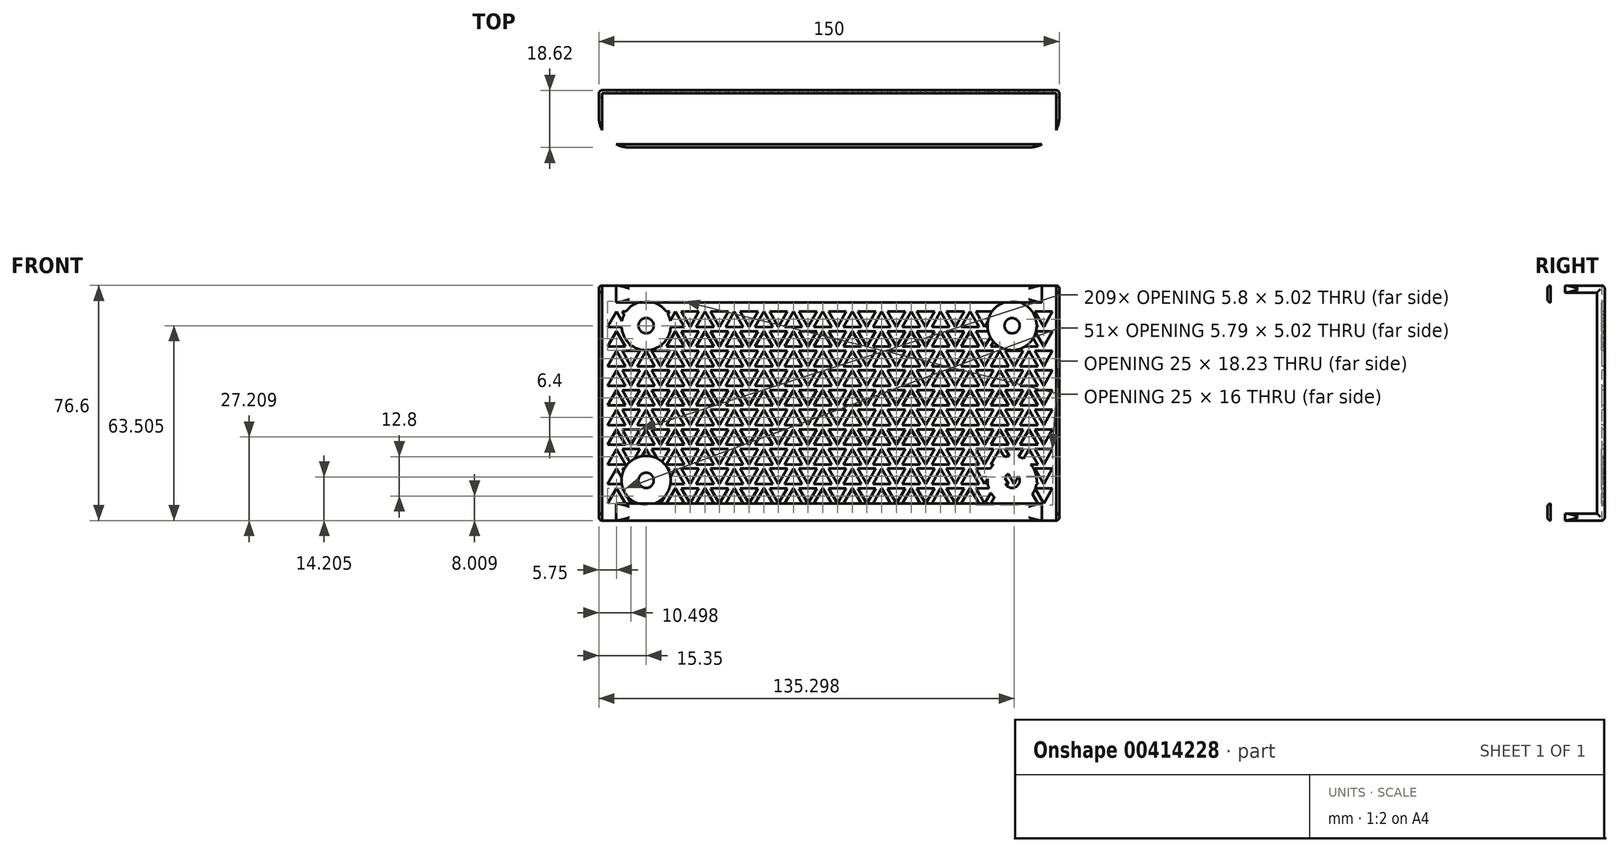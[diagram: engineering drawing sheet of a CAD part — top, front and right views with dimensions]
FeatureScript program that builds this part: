
annotation { "Feature Type Name" : "Feature", "Feature Type Description" : "" }
export const myFeature = defineFeature(function(context is Context, id is Id, definition is map)
    precondition{}
    {
        {
            var Q0;
            Q0=qCreatedBy(makeId("Right.planeOp"),FACE);
            var sketch = newSketch(context, id + "F0", { "sketchPlane" : qUnion([Q0])});
            skLineSegment(sketch, "E0", {"start": v(-14.28, -3.2) * mm, "end": v(-0.28, -3.2) * mm});
            skLineSegment(sketch, "E1", {"start": v(-0.28, -3.2) * mm, "end": v(-0.28, 68.8) * mm});
            skLineSegment(sketch, "E2", {"start": v(-14.28, -3.2) * mm, "end": v(-14.28, 0) * mm});
            skLineSegment(sketch, "E3", {"start": v(-0.28, 68.8) * mm, "end": v(2.22, 68.8) * mm});
            skLineSegment(sketch, "E4", {"start": v(2.22, 68.8) * mm, "end": v(2.22, -3.2) * mm});
            skLineSegment(sketch, "E5", {"start": v(2.22, -5.5) * mm, "end": v(-16.4, -5.5) * mm});
            skLineSegment(sketch, "E6", {"start": v(-16.4, -5.5) * mm, "end": v(-16.4, 0) * mm});
            skLineSegment(sketch, "E7", {"start": v(-16.4, 0) * mm, "end": v(-14.28, 0) * mm});
            skLineSegment(sketch, "E8", {"start": v(-0.28, -3.2) * mm, "end": v(2.22, -3.2) * mm});
            skLineSegment(sketch, "E9", {"start": v(-0.28, 32.8) * mm, "end": v(-25.27, 32.8) * mm, "construction": true});
            skPoint(sketch, "E9.endSnap0", {"position": v(-0.28, 32.8) * mm});
            skLineSegment(sketch, "E10", {"start": v(2.22, -3.2) * mm, "end": v(2.22, -5.5) * mm});
            skLineSegment(sketch, "E11.MirrorCS", {"start": v(-16.4, 71.1) * mm, "end": v(-16.4, 65.6) * mm});
            skLineSegment(sketch, "E12.MirrorCS", {"start": v(-16.4, 65.6) * mm, "end": v(-14.28, 65.6) * mm});
            skLineSegment(sketch, "E13.MirrorCS", {"start": v(-14.28, 68.8) * mm, "end": v(-14.28, 65.6) * mm});
            skLineSegment(sketch, "E14.MirrorCS", {"start": v(-14.28, 68.8) * mm, "end": v(-0.28, 68.8) * mm});
            skLineSegment(sketch, "E15.MirrorCS", {"start": v(2.22, 68.8) * mm, "end": v(2.22, 71.1) * mm});
            skLineSegment(sketch, "E16.MirrorCS", {"start": v(2.22, 71.1) * mm, "end": v(-16.4, 71.1) * mm});
            skSolve(sketch);
        }
        {
            var Q0;
            Q0=makeQuery(id+"F0.imprint","IMPRINT",FACE,{"disambiguationData":[TD([[makeQuery(id+"F0.imprint","IMPRINT",EDGE,{"derivedFrom":sQuery(id+"F0.wireOp",EDGE,"E0")}),-1.0]])]});
            var Q1;
            Q1=makeQuery(id+"F0.imprint","IMPRINT",FACE,{"disambiguationData":[TD([[makeQuery(id+"F0.imprint","IMPRINT",EDGE,{"derivedFrom":sQuery(id+"F0.wireOp",EDGE,"E1")}),-1.0]])]});
            var Q2;
            Q2=makeQuery(id+"F0.imprint","IMPRINT",FACE,{"disambiguationData":[TD([[makeQuery(id+"F0.imprint","IMPRINT",EDGE,{"derivedFrom":sQuery(id+"F0.wireOp",EDGE,"E11.MirrorCS")}),1.0]])]});
            extrude(context, id + "F1", {"entities" : qUnion([Q0, Q1, Q2]), "depth" : 150 * mm});
        }
        {
            var Q0;
            Q0=makeQuery(id+"F1.opExtrude","SWEPT_FACE",FACE,{"disambiguationData":[OSD([sQuery(id+"F0.wireOp",EDGE,"E4")])]});
            var sketch = newSketch(context, id + "F2", { "sketchPlane" : qUnion([Q0])});
            skCircle(sketch, "E17.MirrorC", {"center": v(-134.6, 58) * mm, "radius": 2.48 * mm});
            skCircle(sketch, "E18.MirrorC", {"center": v(-134.6, 58) * mm, "radius": 8 * mm});
            skLineSegment(sketch, "E19", {"start": v(0, 32.8) * mm, "end": v(-150, 32.8) * mm, "construction": true});
            skCircle(sketch, "E20.MirrorC", {"center": v(-134.6, 7.6) * mm, "radius": 8 * mm});
            skCircle(sketch, "E21.MirrorC", {"center": v(-134.6, 7.6) * mm, "radius": 2.48 * mm});
            skLineSegment(sketch, "E22", {"start": v(-75, 32.8) * mm, "end": v(-75, -18.93) * mm, "construction": true});
            skCircle(sketch, "E23.MirrorC", {"center": v(-15.4, 58) * mm, "radius": 2.48 * mm});
            skCircle(sketch, "E24.MirrorC", {"center": v(-15.4, 58) * mm, "radius": 8 * mm});
            skCircle(sketch, "E25.MirrorC", {"center": v(-15.4, 7.6) * mm, "radius": 2.48 * mm});
            skCircle(sketch, "E26.MirrorC", {"center": v(-15.4, 7.6) * mm, "radius": 8 * mm});
            skSolve(sketch);
        }
        {
            var Q0;
            {var subQ0=sQuery(id+"F0.wireOp",EDGE,"E1");Q0=makeQuery(id+"FQkC6kYxM6FwjvR_1.boolean.opBoolean","MERGE",FACE,{"derivedFrom":[makeQuery(id+"F1.opExtrude","SWEPT_FACE",FACE,{"disambiguationData":[OSD([subQ0])]}),makeQuery(id+"FQkC6kYxM6FwjvR_1.opExtrude","CAP_FACE",FACE,{"disambiguationData":[OSD([subQ0]),ownerDisambiguation([makeQuery(id+"F2.imprint","IMPRINT",EDGE,{"derivedFrom":sQuery(id+"F2.wireOp",EDGE,"f48PPpMc-yMvx-ferq-ZrUK-wZFvooTv5NzE.bottom")})])],"isStart":false}),makeQuery(id+"FQkC6kYxM6FwjvR_1.opExtrude","CAP_FACE",FACE,{"disambiguationData":[OSD([subQ0]),ownerDisambiguation([makeQuery(id+"F2.imprint","IMPRINT",EDGE,{"derivedFrom":sQuery(id+"F2.wireOp",EDGE,"981fdd8d-e6c7-4c50-9df8-fd8ac8e3de200.MirrorCS")})])],"isStart":false})]});}
            var sketch = newSketch(context, id + "F3", { "sketchPlane" : qUnion([Q0])});
            skLineSegment(sketch, "E27", {"start": v(2.85, 0) * mm, "end": v(8.65, 0) * mm});
            skLineSegment(sketch, "E28", {"start": v(8.65, 0) * mm, "end": v(5.75, 5.02) * mm});
            skLineSegment(sketch, "E29", {"start": v(5.75, 5.02) * mm, "end": v(2.85, 0) * mm});
            skLineSegment(sketch, "E30", {"start": v(7.6, 5.02) * mm, "end": v(13.4, 5.02) * mm});
            skLineSegment(sketch, "E31", {"start": v(13.4, 5.02) * mm, "end": v(10.5, 0) * mm});
            skLineSegment(sketch, "E32", {"start": v(10.5, 0) * mm, "end": v(7.6, 5.02) * mm});
            skLineSegment(sketch, "E33.0.1.0", {"start": v(2.85, 6.4) * mm, "end": v(8.65, 6.4) * mm});
            skLineSegment(sketch, "E33.0.1.1", {"start": v(8.65, 6.4) * mm, "end": v(5.75, 11.42) * mm});
            skLineSegment(sketch, "E33.0.1.2", {"start": v(5.75, 11.42) * mm, "end": v(2.85, 6.4) * mm});
            skLineSegment(sketch, "E33.0.1.3", {"start": v(10.5, 6.4) * mm, "end": v(7.6, 11.42) * mm});
            skLineSegment(sketch, "E33.0.1.4", {"start": v(13.4, 11.42) * mm, "end": v(10.5, 6.4) * mm});
            skLineSegment(sketch, "E33.0.1.5", {"start": v(7.6, 11.42) * mm, "end": v(13.4, 11.42) * mm});
            skLineSegment(sketch, "E33.0.2.0", {"start": v(2.85, 12.8) * mm, "end": v(8.65, 12.8) * mm});
            skLineSegment(sketch, "E33.0.2.1", {"start": v(8.65, 12.8) * mm, "end": v(5.75, 17.82) * mm});
            skLineSegment(sketch, "E33.0.2.2", {"start": v(5.75, 17.82) * mm, "end": v(2.85, 12.8) * mm});
            skLineSegment(sketch, "E33.0.2.3", {"start": v(10.5, 12.8) * mm, "end": v(7.6, 17.82) * mm});
            skLineSegment(sketch, "E33.0.2.4", {"start": v(13.4, 17.82) * mm, "end": v(10.5, 12.8) * mm});
            skLineSegment(sketch, "E33.0.2.5", {"start": v(7.6, 17.82) * mm, "end": v(13.4, 17.82) * mm});
            skLineSegment(sketch, "E33.0.3.0", {"start": v(2.85, 19.2) * mm, "end": v(8.65, 19.2) * mm});
            skLineSegment(sketch, "E33.0.3.1", {"start": v(8.65, 19.2) * mm, "end": v(5.75, 24.22) * mm});
            skLineSegment(sketch, "E33.0.3.2", {"start": v(5.75, 24.22) * mm, "end": v(2.85, 19.2) * mm});
            skLineSegment(sketch, "E33.0.3.3", {"start": v(10.5, 19.2) * mm, "end": v(7.6, 24.22) * mm});
            skLineSegment(sketch, "E33.0.3.4", {"start": v(13.4, 24.22) * mm, "end": v(10.5, 19.2) * mm});
            skLineSegment(sketch, "E33.0.3.5", {"start": v(7.6, 24.22) * mm, "end": v(13.4, 24.22) * mm});
            skLineSegment(sketch, "E33.0.4.0", {"start": v(2.85, 25.6) * mm, "end": v(8.65, 25.6) * mm});
            skLineSegment(sketch, "E33.0.4.1", {"start": v(8.65, 25.6) * mm, "end": v(5.75, 30.62) * mm});
            skLineSegment(sketch, "E33.0.4.2", {"start": v(5.75, 30.62) * mm, "end": v(2.85, 25.6) * mm});
            skLineSegment(sketch, "E33.0.4.3", {"start": v(10.5, 25.6) * mm, "end": v(7.6, 30.62) * mm});
            skLineSegment(sketch, "E33.0.4.4", {"start": v(13.4, 30.62) * mm, "end": v(10.5, 25.6) * mm});
            skLineSegment(sketch, "E33.0.4.5", {"start": v(7.6, 30.62) * mm, "end": v(13.4, 30.62) * mm});
            skLineSegment(sketch, "E33.0.5.0", {"start": v(2.85, 32) * mm, "end": v(8.65, 32) * mm});
            skLineSegment(sketch, "E33.0.5.1", {"start": v(8.65, 32) * mm, "end": v(5.75, 37.02) * mm});
            skLineSegment(sketch, "E33.0.5.2", {"start": v(5.75, 37.02) * mm, "end": v(2.85, 32) * mm});
            skLineSegment(sketch, "E33.0.5.3", {"start": v(10.5, 32) * mm, "end": v(7.6, 37.02) * mm});
            skLineSegment(sketch, "E33.0.5.4", {"start": v(13.4, 37.02) * mm, "end": v(10.5, 32) * mm});
            skLineSegment(sketch, "E33.0.5.5", {"start": v(7.6, 37.02) * mm, "end": v(13.4, 37.02) * mm});
            skLineSegment(sketch, "E33.0.6.0", {"start": v(2.85, 38.4) * mm, "end": v(8.65, 38.4) * mm});
            skLineSegment(sketch, "E33.0.6.1", {"start": v(8.65, 38.4) * mm, "end": v(5.75, 43.42) * mm});
            skLineSegment(sketch, "E33.0.6.2", {"start": v(5.75, 43.42) * mm, "end": v(2.85, 38.4) * mm});
            skLineSegment(sketch, "E33.0.6.3", {"start": v(10.5, 38.4) * mm, "end": v(7.6, 43.42) * mm});
            skLineSegment(sketch, "E33.0.6.4", {"start": v(13.4, 43.42) * mm, "end": v(10.5, 38.4) * mm});
            skLineSegment(sketch, "E33.0.6.5", {"start": v(7.6, 43.42) * mm, "end": v(13.4, 43.42) * mm});
            skLineSegment(sketch, "E33.0.7.0", {"start": v(2.85, 44.8) * mm, "end": v(8.65, 44.8) * mm});
            skLineSegment(sketch, "E33.0.7.1", {"start": v(8.65, 44.8) * mm, "end": v(5.75, 49.82) * mm});
            skLineSegment(sketch, "E33.0.7.2", {"start": v(5.75, 49.82) * mm, "end": v(2.85, 44.8) * mm});
            skLineSegment(sketch, "E33.0.7.3", {"start": v(10.5, 44.8) * mm, "end": v(7.6, 49.82) * mm});
            skLineSegment(sketch, "E33.0.7.4", {"start": v(13.4, 49.82) * mm, "end": v(10.5, 44.8) * mm});
            skLineSegment(sketch, "E33.0.7.5", {"start": v(7.6, 49.82) * mm, "end": v(13.4, 49.82) * mm});
            skLineSegment(sketch, "E33.0.8.0", {"start": v(2.85, 51.2) * mm, "end": v(8.65, 51.2) * mm});
            skLineSegment(sketch, "E33.0.8.1", {"start": v(8.65, 51.2) * mm, "end": v(5.75, 56.22) * mm});
            skLineSegment(sketch, "E33.0.8.2", {"start": v(5.75, 56.22) * mm, "end": v(2.85, 51.2) * mm});
            skLineSegment(sketch, "E33.0.8.3", {"start": v(10.5, 51.2) * mm, "end": v(7.6, 56.22) * mm});
            skLineSegment(sketch, "E33.0.8.4", {"start": v(13.4, 56.22) * mm, "end": v(10.5, 51.2) * mm});
            skLineSegment(sketch, "E33.0.8.5", {"start": v(7.6, 56.22) * mm, "end": v(13.4, 56.22) * mm});
            skLineSegment(sketch, "E33.0.9.0", {"start": v(2.85, 57.6) * mm, "end": v(8.65, 57.6) * mm});
            skLineSegment(sketch, "E33.0.9.1", {"start": v(8.65, 57.6) * mm, "end": v(5.75, 62.62) * mm});
            skLineSegment(sketch, "E33.0.9.2", {"start": v(5.75, 62.62) * mm, "end": v(2.85, 57.6) * mm});
            skLineSegment(sketch, "E33.0.9.3", {"start": v(10.5, 57.6) * mm, "end": v(7.6, 62.62) * mm});
            skLineSegment(sketch, "E33.0.9.4", {"start": v(13.4, 62.62) * mm, "end": v(10.5, 57.6) * mm});
            skLineSegment(sketch, "E33.0.9.5", {"start": v(7.6, 62.62) * mm, "end": v(13.4, 62.62) * mm});
            skLineSegment(sketch, "E33.1.0.0", {"start": v(12.45, 0) * mm, "end": v(18.25, 0) * mm});
            skLineSegment(sketch, "E33.1.0.1", {"start": v(18.25, 0) * mm, "end": v(15.35, 5.02) * mm});
            skLineSegment(sketch, "E33.1.0.2", {"start": v(15.35, 5.02) * mm, "end": v(12.45, 0) * mm});
            skLineSegment(sketch, "E33.1.0.3", {"start": v(20.1, 0) * mm, "end": v(17.2, 5.02) * mm});
            skLineSegment(sketch, "E33.1.0.4", {"start": v(23, 5.02) * mm, "end": v(20.1, 0) * mm});
            skLineSegment(sketch, "E33.1.0.5", {"start": v(17.2, 5.02) * mm, "end": v(23, 5.02) * mm});
            skLineSegment(sketch, "E33.1.1.0", {"start": v(12.45, 6.4) * mm, "end": v(18.25, 6.4) * mm});
            skLineSegment(sketch, "E33.1.1.1", {"start": v(18.25, 6.4) * mm, "end": v(15.35, 11.42) * mm});
            skLineSegment(sketch, "E33.1.1.2", {"start": v(15.35, 11.42) * mm, "end": v(12.45, 6.4) * mm});
            skLineSegment(sketch, "E33.1.1.3", {"start": v(20.1, 6.4) * mm, "end": v(17.2, 11.42) * mm});
            skLineSegment(sketch, "E33.1.1.4", {"start": v(23, 11.42) * mm, "end": v(20.1, 6.4) * mm});
            skLineSegment(sketch, "E33.1.1.5", {"start": v(17.2, 11.42) * mm, "end": v(23, 11.42) * mm});
            skLineSegment(sketch, "E33.1.2.0", {"start": v(12.45, 12.8) * mm, "end": v(18.25, 12.8) * mm});
            skLineSegment(sketch, "E33.1.2.1", {"start": v(18.25, 12.8) * mm, "end": v(15.35, 17.82) * mm});
            skLineSegment(sketch, "E33.1.2.2", {"start": v(15.35, 17.82) * mm, "end": v(12.45, 12.8) * mm});
            skLineSegment(sketch, "E33.1.2.3", {"start": v(20.1, 12.8) * mm, "end": v(17.2, 17.82) * mm});
            skLineSegment(sketch, "E33.1.2.4", {"start": v(23, 17.82) * mm, "end": v(20.1, 12.8) * mm});
            skLineSegment(sketch, "E33.1.2.5", {"start": v(17.2, 17.82) * mm, "end": v(23, 17.82) * mm});
            skLineSegment(sketch, "E33.1.3.0", {"start": v(12.45, 19.2) * mm, "end": v(18.25, 19.2) * mm});
            skLineSegment(sketch, "E33.1.3.1", {"start": v(18.25, 19.2) * mm, "end": v(15.35, 24.22) * mm});
            skLineSegment(sketch, "E33.1.3.2", {"start": v(15.35, 24.22) * mm, "end": v(12.45, 19.2) * mm});
            skLineSegment(sketch, "E33.1.3.3", {"start": v(20.1, 19.2) * mm, "end": v(17.2, 24.22) * mm});
            skLineSegment(sketch, "E33.1.3.4", {"start": v(23, 24.22) * mm, "end": v(20.1, 19.2) * mm});
            skLineSegment(sketch, "E33.1.3.5", {"start": v(17.2, 24.22) * mm, "end": v(23, 24.22) * mm});
            skLineSegment(sketch, "E33.1.4.0", {"start": v(12.45, 25.6) * mm, "end": v(18.25, 25.6) * mm});
            skLineSegment(sketch, "E33.1.4.1", {"start": v(18.25, 25.6) * mm, "end": v(15.35, 30.62) * mm});
            skLineSegment(sketch, "E33.1.4.2", {"start": v(15.35, 30.62) * mm, "end": v(12.45, 25.6) * mm});
            skLineSegment(sketch, "E33.1.4.3", {"start": v(20.1, 25.6) * mm, "end": v(17.2, 30.62) * mm});
            skLineSegment(sketch, "E33.1.4.4", {"start": v(23, 30.62) * mm, "end": v(20.1, 25.6) * mm});
            skLineSegment(sketch, "E33.1.4.5", {"start": v(17.2, 30.62) * mm, "end": v(23, 30.62) * mm});
            skLineSegment(sketch, "E33.1.5.0", {"start": v(12.45, 32) * mm, "end": v(18.25, 32) * mm});
            skLineSegment(sketch, "E33.1.5.1", {"start": v(18.25, 32) * mm, "end": v(15.35, 37.02) * mm});
            skLineSegment(sketch, "E33.1.5.2", {"start": v(15.35, 37.02) * mm, "end": v(12.45, 32) * mm});
            skLineSegment(sketch, "E33.1.5.3", {"start": v(20.1, 32) * mm, "end": v(17.2, 37.02) * mm});
            skLineSegment(sketch, "E33.1.5.4", {"start": v(23, 37.02) * mm, "end": v(20.1, 32) * mm});
            skLineSegment(sketch, "E33.1.5.5", {"start": v(17.2, 37.02) * mm, "end": v(23, 37.02) * mm});
            skLineSegment(sketch, "E33.1.6.0", {"start": v(12.45, 38.4) * mm, "end": v(18.25, 38.4) * mm});
            skLineSegment(sketch, "E33.1.6.1", {"start": v(18.25, 38.4) * mm, "end": v(15.35, 43.42) * mm});
            skLineSegment(sketch, "E33.1.6.2", {"start": v(15.35, 43.42) * mm, "end": v(12.45, 38.4) * mm});
            skLineSegment(sketch, "E33.1.6.3", {"start": v(20.1, 38.4) * mm, "end": v(17.2, 43.42) * mm});
            skLineSegment(sketch, "E33.1.6.4", {"start": v(23, 43.42) * mm, "end": v(20.1, 38.4) * mm});
            skLineSegment(sketch, "E33.1.6.5", {"start": v(17.2, 43.42) * mm, "end": v(23, 43.42) * mm});
            skLineSegment(sketch, "E33.1.7.0", {"start": v(12.45, 44.8) * mm, "end": v(18.25, 44.8) * mm});
            skLineSegment(sketch, "E33.1.7.1", {"start": v(18.25, 44.8) * mm, "end": v(15.35, 49.82) * mm});
            skLineSegment(sketch, "E33.1.7.2", {"start": v(15.35, 49.82) * mm, "end": v(12.45, 44.8) * mm});
            skLineSegment(sketch, "E33.1.7.3", {"start": v(20.1, 44.8) * mm, "end": v(17.2, 49.82) * mm});
            skLineSegment(sketch, "E33.1.7.4", {"start": v(23, 49.82) * mm, "end": v(20.1, 44.8) * mm});
            skLineSegment(sketch, "E33.1.7.5", {"start": v(17.2, 49.82) * mm, "end": v(23, 49.82) * mm});
            skLineSegment(sketch, "E33.1.8.0", {"start": v(12.45, 51.2) * mm, "end": v(18.25, 51.2) * mm});
            skLineSegment(sketch, "E33.1.8.1", {"start": v(18.25, 51.2) * mm, "end": v(15.35, 56.22) * mm});
            skLineSegment(sketch, "E33.1.8.2", {"start": v(15.35, 56.22) * mm, "end": v(12.45, 51.2) * mm});
            skLineSegment(sketch, "E33.1.8.3", {"start": v(20.1, 51.2) * mm, "end": v(17.2, 56.22) * mm});
            skLineSegment(sketch, "E33.1.8.4", {"start": v(23, 56.22) * mm, "end": v(20.1, 51.2) * mm});
            skLineSegment(sketch, "E33.1.8.5", {"start": v(17.2, 56.22) * mm, "end": v(23, 56.22) * mm});
            skLineSegment(sketch, "E33.1.9.0", {"start": v(12.45, 57.6) * mm, "end": v(18.25, 57.6) * mm});
            skLineSegment(sketch, "E33.1.9.1", {"start": v(18.25, 57.6) * mm, "end": v(15.35, 62.62) * mm});
            skLineSegment(sketch, "E33.1.9.2", {"start": v(15.35, 62.62) * mm, "end": v(12.45, 57.6) * mm});
            skLineSegment(sketch, "E33.1.9.3", {"start": v(20.1, 57.6) * mm, "end": v(17.2, 62.62) * mm});
            skLineSegment(sketch, "E33.1.9.4", {"start": v(23, 62.62) * mm, "end": v(20.1, 57.6) * mm});
            skLineSegment(sketch, "E33.1.9.5", {"start": v(17.2, 62.62) * mm, "end": v(23, 62.62) * mm});
            skLineSegment(sketch, "E33.2.0.0", {"start": v(22.05, 0) * mm, "end": v(27.85, 0) * mm});
            skLineSegment(sketch, "E33.2.0.1", {"start": v(27.85, 0) * mm, "end": v(24.95, 5.02) * mm});
            skLineSegment(sketch, "E33.2.0.2", {"start": v(24.95, 5.02) * mm, "end": v(22.05, 0) * mm});
            skLineSegment(sketch, "E33.2.0.3", {"start": v(29.7, 0) * mm, "end": v(26.8, 5.02) * mm});
            skLineSegment(sketch, "E33.2.0.4", {"start": v(32.6, 5.02) * mm, "end": v(29.7, 0) * mm});
            skLineSegment(sketch, "E33.2.0.5", {"start": v(26.8, 5.02) * mm, "end": v(32.6, 5.02) * mm});
            skLineSegment(sketch, "E33.2.1.0", {"start": v(22.05, 6.4) * mm, "end": v(27.85, 6.4) * mm});
            skLineSegment(sketch, "E33.2.1.1", {"start": v(27.85, 6.4) * mm, "end": v(24.95, 11.42) * mm});
            skLineSegment(sketch, "E33.2.1.2", {"start": v(24.95, 11.42) * mm, "end": v(22.05, 6.4) * mm});
            skLineSegment(sketch, "E33.2.1.3", {"start": v(29.7, 6.4) * mm, "end": v(26.8, 11.42) * mm});
            skLineSegment(sketch, "E33.2.1.4", {"start": v(32.6, 11.42) * mm, "end": v(29.7, 6.4) * mm});
            skLineSegment(sketch, "E33.2.1.5", {"start": v(26.8, 11.42) * mm, "end": v(32.6, 11.42) * mm});
            skLineSegment(sketch, "E33.2.2.0", {"start": v(22.05, 12.8) * mm, "end": v(27.85, 12.8) * mm});
            skLineSegment(sketch, "E33.2.2.1", {"start": v(27.85, 12.8) * mm, "end": v(24.95, 17.82) * mm});
            skLineSegment(sketch, "E33.2.2.2", {"start": v(24.95, 17.82) * mm, "end": v(22.05, 12.8) * mm});
            skLineSegment(sketch, "E33.2.2.3", {"start": v(29.7, 12.8) * mm, "end": v(26.8, 17.82) * mm});
            skLineSegment(sketch, "E33.2.2.4", {"start": v(32.6, 17.82) * mm, "end": v(29.7, 12.8) * mm});
            skLineSegment(sketch, "E33.2.2.5", {"start": v(26.8, 17.82) * mm, "end": v(32.6, 17.82) * mm});
            skLineSegment(sketch, "E33.2.3.0", {"start": v(22.05, 19.2) * mm, "end": v(27.85, 19.2) * mm});
            skLineSegment(sketch, "E33.2.3.1", {"start": v(27.85, 19.2) * mm, "end": v(24.95, 24.22) * mm});
            skLineSegment(sketch, "E33.2.3.2", {"start": v(24.95, 24.22) * mm, "end": v(22.05, 19.2) * mm});
            skLineSegment(sketch, "E33.2.3.3", {"start": v(29.7, 19.2) * mm, "end": v(26.8, 24.22) * mm});
            skLineSegment(sketch, "E33.2.3.4", {"start": v(32.6, 24.22) * mm, "end": v(29.7, 19.2) * mm});
            skLineSegment(sketch, "E33.2.3.5", {"start": v(26.8, 24.22) * mm, "end": v(32.6, 24.22) * mm});
            skLineSegment(sketch, "E33.2.4.0", {"start": v(22.05, 25.6) * mm, "end": v(27.85, 25.6) * mm});
            skLineSegment(sketch, "E33.2.4.1", {"start": v(27.85, 25.6) * mm, "end": v(24.95, 30.62) * mm});
            skLineSegment(sketch, "E33.2.4.2", {"start": v(24.95, 30.62) * mm, "end": v(22.05, 25.6) * mm});
            skLineSegment(sketch, "E33.2.4.3", {"start": v(29.7, 25.6) * mm, "end": v(26.8, 30.62) * mm});
            skLineSegment(sketch, "E33.2.4.4", {"start": v(32.6, 30.62) * mm, "end": v(29.7, 25.6) * mm});
            skLineSegment(sketch, "E33.2.4.5", {"start": v(26.8, 30.62) * mm, "end": v(32.6, 30.62) * mm});
            skLineSegment(sketch, "E33.2.5.0", {"start": v(22.05, 32) * mm, "end": v(27.85, 32) * mm});
            skLineSegment(sketch, "E33.2.5.1", {"start": v(27.85, 32) * mm, "end": v(24.95, 37.02) * mm});
            skLineSegment(sketch, "E33.2.5.2", {"start": v(24.95, 37.02) * mm, "end": v(22.05, 32) * mm});
            skLineSegment(sketch, "E33.2.5.3", {"start": v(29.7, 32) * mm, "end": v(26.8, 37.02) * mm});
            skLineSegment(sketch, "E33.2.5.4", {"start": v(32.6, 37.02) * mm, "end": v(29.7, 32) * mm});
            skLineSegment(sketch, "E33.2.5.5", {"start": v(26.8, 37.02) * mm, "end": v(32.6, 37.02) * mm});
            skLineSegment(sketch, "E33.2.6.0", {"start": v(22.05, 38.4) * mm, "end": v(27.85, 38.4) * mm});
            skLineSegment(sketch, "E33.2.6.1", {"start": v(27.85, 38.4) * mm, "end": v(24.95, 43.42) * mm});
            skLineSegment(sketch, "E33.2.6.2", {"start": v(24.95, 43.42) * mm, "end": v(22.05, 38.4) * mm});
            skLineSegment(sketch, "E33.2.6.3", {"start": v(29.7, 38.4) * mm, "end": v(26.8, 43.42) * mm});
            skLineSegment(sketch, "E33.2.6.4", {"start": v(32.6, 43.42) * mm, "end": v(29.7, 38.4) * mm});
            skLineSegment(sketch, "E33.2.6.5", {"start": v(26.8, 43.42) * mm, "end": v(32.6, 43.42) * mm});
            skLineSegment(sketch, "E33.2.7.0", {"start": v(22.05, 44.8) * mm, "end": v(27.85, 44.8) * mm});
            skLineSegment(sketch, "E33.2.7.1", {"start": v(27.85, 44.8) * mm, "end": v(24.95, 49.82) * mm});
            skLineSegment(sketch, "E33.2.7.2", {"start": v(24.95, 49.82) * mm, "end": v(22.05, 44.8) * mm});
            skLineSegment(sketch, "E33.2.7.3", {"start": v(29.7, 44.8) * mm, "end": v(26.8, 49.82) * mm});
            skLineSegment(sketch, "E33.2.7.4", {"start": v(32.6, 49.82) * mm, "end": v(29.7, 44.8) * mm});
            skLineSegment(sketch, "E33.2.7.5", {"start": v(26.8, 49.82) * mm, "end": v(32.6, 49.82) * mm});
            skLineSegment(sketch, "E33.2.8.0", {"start": v(22.05, 51.2) * mm, "end": v(27.85, 51.2) * mm});
            skLineSegment(sketch, "E33.2.8.1", {"start": v(27.85, 51.2) * mm, "end": v(24.95, 56.22) * mm});
            skLineSegment(sketch, "E33.2.8.2", {"start": v(24.95, 56.22) * mm, "end": v(22.05, 51.2) * mm});
            skLineSegment(sketch, "E33.2.8.3", {"start": v(29.7, 51.2) * mm, "end": v(26.8, 56.22) * mm});
            skLineSegment(sketch, "E33.2.8.4", {"start": v(32.6, 56.22) * mm, "end": v(29.7, 51.2) * mm});
            skLineSegment(sketch, "E33.2.8.5", {"start": v(26.8, 56.22) * mm, "end": v(32.6, 56.22) * mm});
            skLineSegment(sketch, "E33.2.9.0", {"start": v(22.05, 57.6) * mm, "end": v(27.85, 57.6) * mm});
            skLineSegment(sketch, "E33.2.9.1", {"start": v(27.85, 57.6) * mm, "end": v(24.95, 62.62) * mm});
            skLineSegment(sketch, "E33.2.9.2", {"start": v(24.95, 62.62) * mm, "end": v(22.05, 57.6) * mm});
            skLineSegment(sketch, "E33.2.9.3", {"start": v(29.7, 57.6) * mm, "end": v(26.8, 62.62) * mm});
            skLineSegment(sketch, "E33.2.9.4", {"start": v(32.6, 62.62) * mm, "end": v(29.7, 57.6) * mm});
            skLineSegment(sketch, "E33.2.9.5", {"start": v(26.8, 62.62) * mm, "end": v(32.6, 62.62) * mm});
            skLineSegment(sketch, "E33.3.0.0", {"start": v(31.65, 0) * mm, "end": v(37.45, 0) * mm});
            skLineSegment(sketch, "E33.3.0.1", {"start": v(37.45, 0) * mm, "end": v(34.55, 5.02) * mm});
            skLineSegment(sketch, "E33.3.0.2", {"start": v(34.55, 5.02) * mm, "end": v(31.65, 0) * mm});
            skLineSegment(sketch, "E33.3.0.3", {"start": v(39.3, 0) * mm, "end": v(36.4, 5.02) * mm});
            skLineSegment(sketch, "E33.3.0.4", {"start": v(42.2, 5.02) * mm, "end": v(39.3, 0) * mm});
            skLineSegment(sketch, "E33.3.0.5", {"start": v(36.4, 5.02) * mm, "end": v(42.2, 5.02) * mm});
            skLineSegment(sketch, "E33.3.1.0", {"start": v(31.65, 6.4) * mm, "end": v(37.45, 6.4) * mm});
            skLineSegment(sketch, "E33.3.1.1", {"start": v(37.45, 6.4) * mm, "end": v(34.55, 11.42) * mm});
            skLineSegment(sketch, "E33.3.1.2", {"start": v(34.55, 11.42) * mm, "end": v(31.65, 6.4) * mm});
            skLineSegment(sketch, "E33.3.1.3", {"start": v(39.3, 6.4) * mm, "end": v(36.4, 11.42) * mm});
            skLineSegment(sketch, "E33.3.1.4", {"start": v(42.2, 11.42) * mm, "end": v(39.3, 6.4) * mm});
            skLineSegment(sketch, "E33.3.1.5", {"start": v(36.4, 11.42) * mm, "end": v(42.2, 11.42) * mm});
            skLineSegment(sketch, "E33.3.2.0", {"start": v(31.65, 12.8) * mm, "end": v(37.45, 12.8) * mm});
            skLineSegment(sketch, "E33.3.2.1", {"start": v(37.45, 12.8) * mm, "end": v(34.55, 17.82) * mm});
            skLineSegment(sketch, "E33.3.2.2", {"start": v(34.55, 17.82) * mm, "end": v(31.65, 12.8) * mm});
            skLineSegment(sketch, "E33.3.2.3", {"start": v(39.3, 12.8) * mm, "end": v(36.4, 17.82) * mm});
            skLineSegment(sketch, "E33.3.2.4", {"start": v(42.2, 17.82) * mm, "end": v(39.3, 12.8) * mm});
            skLineSegment(sketch, "E33.3.2.5", {"start": v(36.4, 17.82) * mm, "end": v(42.2, 17.82) * mm});
            skLineSegment(sketch, "E33.3.3.0", {"start": v(31.65, 19.2) * mm, "end": v(37.45, 19.2) * mm});
            skLineSegment(sketch, "E33.3.3.1", {"start": v(37.45, 19.2) * mm, "end": v(34.55, 24.22) * mm});
            skLineSegment(sketch, "E33.3.3.2", {"start": v(34.55, 24.22) * mm, "end": v(31.65, 19.2) * mm});
            skLineSegment(sketch, "E33.3.3.3", {"start": v(39.3, 19.2) * mm, "end": v(36.4, 24.22) * mm});
            skLineSegment(sketch, "E33.3.3.4", {"start": v(42.2, 24.22) * mm, "end": v(39.3, 19.2) * mm});
            skLineSegment(sketch, "E33.3.3.5", {"start": v(36.4, 24.22) * mm, "end": v(42.2, 24.22) * mm});
            skLineSegment(sketch, "E33.3.4.0", {"start": v(31.65, 25.6) * mm, "end": v(37.45, 25.6) * mm});
            skLineSegment(sketch, "E33.3.4.1", {"start": v(37.45, 25.6) * mm, "end": v(34.55, 30.62) * mm});
            skLineSegment(sketch, "E33.3.4.2", {"start": v(34.55, 30.62) * mm, "end": v(31.65, 25.6) * mm});
            skLineSegment(sketch, "E33.3.4.3", {"start": v(39.3, 25.6) * mm, "end": v(36.4, 30.62) * mm});
            skLineSegment(sketch, "E33.3.4.4", {"start": v(42.2, 30.62) * mm, "end": v(39.3, 25.6) * mm});
            skLineSegment(sketch, "E33.3.4.5", {"start": v(36.4, 30.62) * mm, "end": v(42.2, 30.62) * mm});
            skLineSegment(sketch, "E33.3.5.0", {"start": v(31.65, 32) * mm, "end": v(37.45, 32) * mm});
            skLineSegment(sketch, "E33.3.5.1", {"start": v(37.45, 32) * mm, "end": v(34.55, 37.02) * mm});
            skLineSegment(sketch, "E33.3.5.2", {"start": v(34.55, 37.02) * mm, "end": v(31.65, 32) * mm});
            skLineSegment(sketch, "E33.3.5.3", {"start": v(39.3, 32) * mm, "end": v(36.4, 37.02) * mm});
            skLineSegment(sketch, "E33.3.5.4", {"start": v(42.2, 37.02) * mm, "end": v(39.3, 32) * mm});
            skLineSegment(sketch, "E33.3.5.5", {"start": v(36.4, 37.02) * mm, "end": v(42.2, 37.02) * mm});
            skLineSegment(sketch, "E33.3.6.0", {"start": v(31.65, 38.4) * mm, "end": v(37.45, 38.4) * mm});
            skLineSegment(sketch, "E33.3.6.1", {"start": v(37.45, 38.4) * mm, "end": v(34.55, 43.42) * mm});
            skLineSegment(sketch, "E33.3.6.2", {"start": v(34.55, 43.42) * mm, "end": v(31.65, 38.4) * mm});
            skLineSegment(sketch, "E33.3.6.3", {"start": v(39.3, 38.4) * mm, "end": v(36.4, 43.42) * mm});
            skLineSegment(sketch, "E33.3.6.4", {"start": v(42.2, 43.42) * mm, "end": v(39.3, 38.4) * mm});
            skLineSegment(sketch, "E33.3.6.5", {"start": v(36.4, 43.42) * mm, "end": v(42.2, 43.42) * mm});
            skLineSegment(sketch, "E33.3.7.0", {"start": v(31.65, 44.8) * mm, "end": v(37.45, 44.8) * mm});
            skLineSegment(sketch, "E33.3.7.1", {"start": v(37.45, 44.8) * mm, "end": v(34.55, 49.82) * mm});
            skLineSegment(sketch, "E33.3.7.2", {"start": v(34.55, 49.82) * mm, "end": v(31.65, 44.8) * mm});
            skLineSegment(sketch, "E33.3.7.3", {"start": v(39.3, 44.8) * mm, "end": v(36.4, 49.82) * mm});
            skLineSegment(sketch, "E33.3.7.4", {"start": v(42.2, 49.82) * mm, "end": v(39.3, 44.8) * mm});
            skLineSegment(sketch, "E33.3.7.5", {"start": v(36.4, 49.82) * mm, "end": v(42.2, 49.82) * mm});
            skLineSegment(sketch, "E33.3.8.0", {"start": v(31.65, 51.2) * mm, "end": v(37.45, 51.2) * mm});
            skLineSegment(sketch, "E33.3.8.1", {"start": v(37.45, 51.2) * mm, "end": v(34.55, 56.22) * mm});
            skLineSegment(sketch, "E33.3.8.2", {"start": v(34.55, 56.22) * mm, "end": v(31.65, 51.2) * mm});
            skLineSegment(sketch, "E33.3.8.3", {"start": v(39.3, 51.2) * mm, "end": v(36.4, 56.22) * mm});
            skLineSegment(sketch, "E33.3.8.4", {"start": v(42.2, 56.22) * mm, "end": v(39.3, 51.2) * mm});
            skLineSegment(sketch, "E33.3.8.5", {"start": v(36.4, 56.22) * mm, "end": v(42.2, 56.22) * mm});
            skLineSegment(sketch, "E33.3.9.0", {"start": v(31.65, 57.6) * mm, "end": v(37.45, 57.6) * mm});
            skLineSegment(sketch, "E33.3.9.1", {"start": v(37.45, 57.6) * mm, "end": v(34.55, 62.62) * mm});
            skLineSegment(sketch, "E33.3.9.2", {"start": v(34.55, 62.62) * mm, "end": v(31.65, 57.6) * mm});
            skLineSegment(sketch, "E33.3.9.3", {"start": v(39.3, 57.6) * mm, "end": v(36.4, 62.62) * mm});
            skLineSegment(sketch, "E33.3.9.4", {"start": v(42.2, 62.62) * mm, "end": v(39.3, 57.6) * mm});
            skLineSegment(sketch, "E33.3.9.5", {"start": v(36.4, 62.62) * mm, "end": v(42.2, 62.62) * mm});
            skLineSegment(sketch, "E33.4.0.0", {"start": v(41.25, 0) * mm, "end": v(47.05, 0) * mm});
            skLineSegment(sketch, "E33.4.0.1", {"start": v(47.05, 0) * mm, "end": v(44.15, 5.02) * mm});
            skLineSegment(sketch, "E33.4.0.2", {"start": v(44.15, 5.02) * mm, "end": v(41.25, 0) * mm});
            skLineSegment(sketch, "E33.4.0.3", {"start": v(48.9, 0) * mm, "end": v(46, 5.02) * mm});
            skLineSegment(sketch, "E33.4.0.4", {"start": v(51.8, 5.02) * mm, "end": v(48.9, 0) * mm});
            skLineSegment(sketch, "E33.4.0.5", {"start": v(46, 5.02) * mm, "end": v(51.8, 5.02) * mm});
            skLineSegment(sketch, "E33.4.1.0", {"start": v(41.25, 6.4) * mm, "end": v(47.05, 6.4) * mm});
            skLineSegment(sketch, "E33.4.1.1", {"start": v(47.05, 6.4) * mm, "end": v(44.15, 11.42) * mm});
            skLineSegment(sketch, "E33.4.1.2", {"start": v(44.15, 11.42) * mm, "end": v(41.25, 6.4) * mm});
            skLineSegment(sketch, "E33.4.1.3", {"start": v(48.9, 6.4) * mm, "end": v(46, 11.42) * mm});
            skLineSegment(sketch, "E33.4.1.4", {"start": v(51.8, 11.42) * mm, "end": v(48.9, 6.4) * mm});
            skLineSegment(sketch, "E33.4.1.5", {"start": v(46, 11.42) * mm, "end": v(51.8, 11.42) * mm});
            skLineSegment(sketch, "E33.4.2.0", {"start": v(41.25, 12.8) * mm, "end": v(47.05, 12.8) * mm});
            skLineSegment(sketch, "E33.4.2.1", {"start": v(47.05, 12.8) * mm, "end": v(44.15, 17.82) * mm});
            skLineSegment(sketch, "E33.4.2.2", {"start": v(44.15, 17.82) * mm, "end": v(41.25, 12.8) * mm});
            skLineSegment(sketch, "E33.4.2.3", {"start": v(48.9, 12.8) * mm, "end": v(46, 17.82) * mm});
            skLineSegment(sketch, "E33.4.2.4", {"start": v(51.8, 17.82) * mm, "end": v(48.9, 12.8) * mm});
            skLineSegment(sketch, "E33.4.2.5", {"start": v(46, 17.82) * mm, "end": v(51.8, 17.82) * mm});
            skLineSegment(sketch, "E33.4.3.0", {"start": v(41.25, 19.2) * mm, "end": v(47.05, 19.2) * mm});
            skLineSegment(sketch, "E33.4.3.1", {"start": v(47.05, 19.2) * mm, "end": v(44.15, 24.22) * mm});
            skLineSegment(sketch, "E33.4.3.2", {"start": v(44.15, 24.22) * mm, "end": v(41.25, 19.2) * mm});
            skLineSegment(sketch, "E33.4.3.3", {"start": v(48.9, 19.2) * mm, "end": v(46, 24.22) * mm});
            skLineSegment(sketch, "E33.4.3.4", {"start": v(51.8, 24.22) * mm, "end": v(48.9, 19.2) * mm});
            skLineSegment(sketch, "E33.4.3.5", {"start": v(46, 24.22) * mm, "end": v(51.8, 24.22) * mm});
            skLineSegment(sketch, "E33.4.4.0", {"start": v(41.25, 25.6) * mm, "end": v(47.05, 25.6) * mm});
            skLineSegment(sketch, "E33.4.4.1", {"start": v(47.05, 25.6) * mm, "end": v(44.15, 30.62) * mm});
            skLineSegment(sketch, "E33.4.4.2", {"start": v(44.15, 30.62) * mm, "end": v(41.25, 25.6) * mm});
            skLineSegment(sketch, "E33.4.4.3", {"start": v(48.9, 25.6) * mm, "end": v(46, 30.62) * mm});
            skLineSegment(sketch, "E33.4.4.4", {"start": v(51.8, 30.62) * mm, "end": v(48.9, 25.6) * mm});
            skLineSegment(sketch, "E33.4.4.5", {"start": v(46, 30.62) * mm, "end": v(51.8, 30.62) * mm});
            skLineSegment(sketch, "E33.4.5.0", {"start": v(41.25, 32) * mm, "end": v(47.05, 32) * mm});
            skLineSegment(sketch, "E33.4.5.1", {"start": v(47.05, 32) * mm, "end": v(44.15, 37.02) * mm});
            skLineSegment(sketch, "E33.4.5.2", {"start": v(44.15, 37.02) * mm, "end": v(41.25, 32) * mm});
            skLineSegment(sketch, "E33.4.5.3", {"start": v(48.9, 32) * mm, "end": v(46, 37.02) * mm});
            skLineSegment(sketch, "E33.4.5.4", {"start": v(51.8, 37.02) * mm, "end": v(48.9, 32) * mm});
            skLineSegment(sketch, "E33.4.5.5", {"start": v(46, 37.02) * mm, "end": v(51.8, 37.02) * mm});
            skLineSegment(sketch, "E33.4.6.0", {"start": v(41.25, 38.4) * mm, "end": v(47.05, 38.4) * mm});
            skLineSegment(sketch, "E33.4.6.1", {"start": v(47.05, 38.4) * mm, "end": v(44.15, 43.42) * mm});
            skLineSegment(sketch, "E33.4.6.2", {"start": v(44.15, 43.42) * mm, "end": v(41.25, 38.4) * mm});
            skLineSegment(sketch, "E33.4.6.3", {"start": v(48.9, 38.4) * mm, "end": v(46, 43.42) * mm});
            skLineSegment(sketch, "E33.4.6.4", {"start": v(51.8, 43.42) * mm, "end": v(48.9, 38.4) * mm});
            skLineSegment(sketch, "E33.4.6.5", {"start": v(46, 43.42) * mm, "end": v(51.8, 43.42) * mm});
            skLineSegment(sketch, "E33.4.7.0", {"start": v(41.25, 44.8) * mm, "end": v(47.05, 44.8) * mm});
            skLineSegment(sketch, "E33.4.7.1", {"start": v(47.05, 44.8) * mm, "end": v(44.15, 49.82) * mm});
            skLineSegment(sketch, "E33.4.7.2", {"start": v(44.15, 49.82) * mm, "end": v(41.25, 44.8) * mm});
            skLineSegment(sketch, "E33.4.7.3", {"start": v(48.9, 44.8) * mm, "end": v(46, 49.82) * mm});
            skLineSegment(sketch, "E33.4.7.4", {"start": v(51.8, 49.82) * mm, "end": v(48.9, 44.8) * mm});
            skLineSegment(sketch, "E33.4.7.5", {"start": v(46, 49.82) * mm, "end": v(51.8, 49.82) * mm});
            skLineSegment(sketch, "E33.4.8.0", {"start": v(41.25, 51.2) * mm, "end": v(47.05, 51.2) * mm});
            skLineSegment(sketch, "E33.4.8.1", {"start": v(47.05, 51.2) * mm, "end": v(44.15, 56.22) * mm});
            skLineSegment(sketch, "E33.4.8.2", {"start": v(44.15, 56.22) * mm, "end": v(41.25, 51.2) * mm});
            skLineSegment(sketch, "E33.4.8.3", {"start": v(48.9, 51.2) * mm, "end": v(46, 56.22) * mm});
            skLineSegment(sketch, "E33.4.8.4", {"start": v(51.8, 56.22) * mm, "end": v(48.9, 51.2) * mm});
            skLineSegment(sketch, "E33.4.8.5", {"start": v(46, 56.22) * mm, "end": v(51.8, 56.22) * mm});
            skLineSegment(sketch, "E33.4.9.0", {"start": v(41.25, 57.6) * mm, "end": v(47.05, 57.6) * mm});
            skLineSegment(sketch, "E33.4.9.1", {"start": v(47.05, 57.6) * mm, "end": v(44.15, 62.62) * mm});
            skLineSegment(sketch, "E33.4.9.2", {"start": v(44.15, 62.62) * mm, "end": v(41.25, 57.6) * mm});
            skLineSegment(sketch, "E33.4.9.3", {"start": v(48.9, 57.6) * mm, "end": v(46, 62.62) * mm});
            skLineSegment(sketch, "E33.4.9.4", {"start": v(51.8, 62.62) * mm, "end": v(48.9, 57.6) * mm});
            skLineSegment(sketch, "E33.4.9.5", {"start": v(46, 62.62) * mm, "end": v(51.8, 62.62) * mm});
            skLineSegment(sketch, "E33.5.0.0", {"start": v(50.85, 0) * mm, "end": v(56.65, 0) * mm});
            skLineSegment(sketch, "E33.5.0.1", {"start": v(56.65, 0) * mm, "end": v(53.75, 5.02) * mm});
            skLineSegment(sketch, "E33.5.0.2", {"start": v(53.75, 5.02) * mm, "end": v(50.85, 0) * mm});
            skLineSegment(sketch, "E33.5.0.3", {"start": v(58.5, 0) * mm, "end": v(55.6, 5.02) * mm});
            skLineSegment(sketch, "E33.5.0.4", {"start": v(61.4, 5.02) * mm, "end": v(58.5, 0) * mm});
            skLineSegment(sketch, "E33.5.0.5", {"start": v(55.6, 5.02) * mm, "end": v(61.4, 5.02) * mm});
            skLineSegment(sketch, "E33.5.1.0", {"start": v(50.85, 6.4) * mm, "end": v(56.65, 6.4) * mm});
            skLineSegment(sketch, "E33.5.1.1", {"start": v(56.65, 6.4) * mm, "end": v(53.75, 11.42) * mm});
            skLineSegment(sketch, "E33.5.1.2", {"start": v(53.75, 11.42) * mm, "end": v(50.85, 6.4) * mm});
            skLineSegment(sketch, "E33.5.1.3", {"start": v(58.5, 6.4) * mm, "end": v(55.6, 11.42) * mm});
            skLineSegment(sketch, "E33.5.1.4", {"start": v(61.4, 11.42) * mm, "end": v(58.5, 6.4) * mm});
            skLineSegment(sketch, "E33.5.1.5", {"start": v(55.6, 11.42) * mm, "end": v(61.4, 11.42) * mm});
            skLineSegment(sketch, "E33.5.2.0", {"start": v(50.85, 12.8) * mm, "end": v(56.65, 12.8) * mm});
            skLineSegment(sketch, "E33.5.2.1", {"start": v(56.65, 12.8) * mm, "end": v(53.75, 17.82) * mm});
            skLineSegment(sketch, "E33.5.2.2", {"start": v(53.75, 17.82) * mm, "end": v(50.85, 12.8) * mm});
            skLineSegment(sketch, "E33.5.2.3", {"start": v(58.5, 12.8) * mm, "end": v(55.6, 17.82) * mm});
            skLineSegment(sketch, "E33.5.2.4", {"start": v(61.4, 17.82) * mm, "end": v(58.5, 12.8) * mm});
            skLineSegment(sketch, "E33.5.2.5", {"start": v(55.6, 17.82) * mm, "end": v(61.4, 17.82) * mm});
            skLineSegment(sketch, "E33.5.3.0", {"start": v(50.85, 19.2) * mm, "end": v(56.65, 19.2) * mm});
            skLineSegment(sketch, "E33.5.3.1", {"start": v(56.65, 19.2) * mm, "end": v(53.75, 24.22) * mm});
            skLineSegment(sketch, "E33.5.3.2", {"start": v(53.75, 24.22) * mm, "end": v(50.85, 19.2) * mm});
            skLineSegment(sketch, "E33.5.3.3", {"start": v(58.5, 19.2) * mm, "end": v(55.6, 24.22) * mm});
            skLineSegment(sketch, "E33.5.3.4", {"start": v(61.4, 24.22) * mm, "end": v(58.5, 19.2) * mm});
            skLineSegment(sketch, "E33.5.3.5", {"start": v(55.6, 24.22) * mm, "end": v(61.4, 24.22) * mm});
            skLineSegment(sketch, "E33.5.4.0", {"start": v(50.85, 25.6) * mm, "end": v(56.65, 25.6) * mm});
            skLineSegment(sketch, "E33.5.4.1", {"start": v(56.65, 25.6) * mm, "end": v(53.75, 30.62) * mm});
            skLineSegment(sketch, "E33.5.4.2", {"start": v(53.75, 30.62) * mm, "end": v(50.85, 25.6) * mm});
            skLineSegment(sketch, "E33.5.4.3", {"start": v(58.5, 25.6) * mm, "end": v(55.6, 30.62) * mm});
            skLineSegment(sketch, "E33.5.4.4", {"start": v(61.4, 30.62) * mm, "end": v(58.5, 25.6) * mm});
            skLineSegment(sketch, "E33.5.4.5", {"start": v(55.6, 30.62) * mm, "end": v(61.4, 30.62) * mm});
            skLineSegment(sketch, "E33.5.5.0", {"start": v(50.85, 32) * mm, "end": v(56.65, 32) * mm});
            skLineSegment(sketch, "E33.5.5.1", {"start": v(56.65, 32) * mm, "end": v(53.75, 37.02) * mm});
            skLineSegment(sketch, "E33.5.5.2", {"start": v(53.75, 37.02) * mm, "end": v(50.85, 32) * mm});
            skLineSegment(sketch, "E33.5.5.3", {"start": v(58.5, 32) * mm, "end": v(55.6, 37.02) * mm});
            skLineSegment(sketch, "E33.5.5.4", {"start": v(61.4, 37.02) * mm, "end": v(58.5, 32) * mm});
            skLineSegment(sketch, "E33.5.5.5", {"start": v(55.6, 37.02) * mm, "end": v(61.4, 37.02) * mm});
            skLineSegment(sketch, "E33.5.6.0", {"start": v(50.85, 38.4) * mm, "end": v(56.65, 38.4) * mm});
            skLineSegment(sketch, "E33.5.6.1", {"start": v(56.65, 38.4) * mm, "end": v(53.75, 43.42) * mm});
            skLineSegment(sketch, "E33.5.6.2", {"start": v(53.75, 43.42) * mm, "end": v(50.85, 38.4) * mm});
            skLineSegment(sketch, "E33.5.6.3", {"start": v(58.5, 38.4) * mm, "end": v(55.6, 43.42) * mm});
            skLineSegment(sketch, "E33.5.6.4", {"start": v(61.4, 43.42) * mm, "end": v(58.5, 38.4) * mm});
            skLineSegment(sketch, "E33.5.6.5", {"start": v(55.6, 43.42) * mm, "end": v(61.4, 43.42) * mm});
            skLineSegment(sketch, "E33.5.7.0", {"start": v(50.85, 44.8) * mm, "end": v(56.65, 44.8) * mm});
            skLineSegment(sketch, "E33.5.7.1", {"start": v(56.65, 44.8) * mm, "end": v(53.75, 49.82) * mm});
            skLineSegment(sketch, "E33.5.7.2", {"start": v(53.75, 49.82) * mm, "end": v(50.85, 44.8) * mm});
            skLineSegment(sketch, "E33.5.7.3", {"start": v(58.5, 44.8) * mm, "end": v(55.6, 49.82) * mm});
            skLineSegment(sketch, "E33.5.7.4", {"start": v(61.4, 49.82) * mm, "end": v(58.5, 44.8) * mm});
            skLineSegment(sketch, "E33.5.7.5", {"start": v(55.6, 49.82) * mm, "end": v(61.4, 49.82) * mm});
            skLineSegment(sketch, "E33.5.8.0", {"start": v(50.85, 51.2) * mm, "end": v(56.65, 51.2) * mm});
            skLineSegment(sketch, "E33.5.8.1", {"start": v(56.65, 51.2) * mm, "end": v(53.75, 56.22) * mm});
            skLineSegment(sketch, "E33.5.8.2", {"start": v(53.75, 56.22) * mm, "end": v(50.85, 51.2) * mm});
            skLineSegment(sketch, "E33.5.8.3", {"start": v(58.5, 51.2) * mm, "end": v(55.6, 56.22) * mm});
            skLineSegment(sketch, "E33.5.8.4", {"start": v(61.4, 56.22) * mm, "end": v(58.5, 51.2) * mm});
            skLineSegment(sketch, "E33.5.8.5", {"start": v(55.6, 56.22) * mm, "end": v(61.4, 56.22) * mm});
            skLineSegment(sketch, "E33.5.9.0", {"start": v(50.85, 57.6) * mm, "end": v(56.65, 57.6) * mm});
            skLineSegment(sketch, "E33.5.9.1", {"start": v(56.65, 57.6) * mm, "end": v(53.75, 62.62) * mm});
            skLineSegment(sketch, "E33.5.9.2", {"start": v(53.75, 62.62) * mm, "end": v(50.85, 57.6) * mm});
            skLineSegment(sketch, "E33.5.9.3", {"start": v(58.5, 57.6) * mm, "end": v(55.6, 62.62) * mm});
            skLineSegment(sketch, "E33.5.9.4", {"start": v(61.4, 62.62) * mm, "end": v(58.5, 57.6) * mm});
            skLineSegment(sketch, "E33.5.9.5", {"start": v(55.6, 62.62) * mm, "end": v(61.4, 62.62) * mm});
            skLineSegment(sketch, "E33.6.0.0", {"start": v(60.45, 0) * mm, "end": v(66.25, 0) * mm});
            skLineSegment(sketch, "E33.6.0.1", {"start": v(66.25, 0) * mm, "end": v(63.35, 5.02) * mm});
            skLineSegment(sketch, "E33.6.0.2", {"start": v(63.35, 5.02) * mm, "end": v(60.45, 0) * mm});
            skLineSegment(sketch, "E33.6.0.3", {"start": v(68.1, 0) * mm, "end": v(65.2, 5.02) * mm});
            skLineSegment(sketch, "E33.6.0.4", {"start": v(71, 5.02) * mm, "end": v(68.1, 0) * mm});
            skLineSegment(sketch, "E33.6.0.5", {"start": v(65.2, 5.02) * mm, "end": v(71, 5.02) * mm});
            skLineSegment(sketch, "E33.6.1.0", {"start": v(60.45, 6.4) * mm, "end": v(66.25, 6.4) * mm});
            skLineSegment(sketch, "E33.6.1.1", {"start": v(66.25, 6.4) * mm, "end": v(63.35, 11.42) * mm});
            skLineSegment(sketch, "E33.6.1.2", {"start": v(63.35, 11.42) * mm, "end": v(60.45, 6.4) * mm});
            skLineSegment(sketch, "E33.6.1.3", {"start": v(68.1, 6.4) * mm, "end": v(65.2, 11.42) * mm});
            skLineSegment(sketch, "E33.6.1.4", {"start": v(71, 11.42) * mm, "end": v(68.1, 6.4) * mm});
            skLineSegment(sketch, "E33.6.1.5", {"start": v(65.2, 11.42) * mm, "end": v(71, 11.42) * mm});
            skLineSegment(sketch, "E33.6.2.0", {"start": v(60.45, 12.8) * mm, "end": v(66.25, 12.8) * mm});
            skLineSegment(sketch, "E33.6.2.1", {"start": v(66.25, 12.8) * mm, "end": v(63.35, 17.82) * mm});
            skLineSegment(sketch, "E33.6.2.2", {"start": v(63.35, 17.82) * mm, "end": v(60.45, 12.8) * mm});
            skLineSegment(sketch, "E33.6.2.3", {"start": v(68.1, 12.8) * mm, "end": v(65.2, 17.82) * mm});
            skLineSegment(sketch, "E33.6.2.4", {"start": v(71, 17.82) * mm, "end": v(68.1, 12.8) * mm});
            skLineSegment(sketch, "E33.6.2.5", {"start": v(65.2, 17.82) * mm, "end": v(71, 17.82) * mm});
            skLineSegment(sketch, "E33.6.3.0", {"start": v(60.45, 19.2) * mm, "end": v(66.25, 19.2) * mm});
            skLineSegment(sketch, "E33.6.3.1", {"start": v(66.25, 19.2) * mm, "end": v(63.35, 24.22) * mm});
            skLineSegment(sketch, "E33.6.3.2", {"start": v(63.35, 24.22) * mm, "end": v(60.45, 19.2) * mm});
            skLineSegment(sketch, "E33.6.3.3", {"start": v(68.1, 19.2) * mm, "end": v(65.2, 24.22) * mm});
            skLineSegment(sketch, "E33.6.3.4", {"start": v(71, 24.22) * mm, "end": v(68.1, 19.2) * mm});
            skLineSegment(sketch, "E33.6.3.5", {"start": v(65.2, 24.22) * mm, "end": v(71, 24.22) * mm});
            skLineSegment(sketch, "E33.6.4.0", {"start": v(60.45, 25.6) * mm, "end": v(66.25, 25.6) * mm});
            skLineSegment(sketch, "E33.6.4.1", {"start": v(66.25, 25.6) * mm, "end": v(63.35, 30.62) * mm});
            skLineSegment(sketch, "E33.6.4.2", {"start": v(63.35, 30.62) * mm, "end": v(60.45, 25.6) * mm});
            skLineSegment(sketch, "E33.6.4.3", {"start": v(68.1, 25.6) * mm, "end": v(65.2, 30.62) * mm});
            skLineSegment(sketch, "E33.6.4.4", {"start": v(71, 30.62) * mm, "end": v(68.1, 25.6) * mm});
            skLineSegment(sketch, "E33.6.4.5", {"start": v(65.2, 30.62) * mm, "end": v(71, 30.62) * mm});
            skLineSegment(sketch, "E33.6.5.0", {"start": v(60.45, 32) * mm, "end": v(66.25, 32) * mm});
            skLineSegment(sketch, "E33.6.5.1", {"start": v(66.25, 32) * mm, "end": v(63.35, 37.02) * mm});
            skLineSegment(sketch, "E33.6.5.2", {"start": v(63.35, 37.02) * mm, "end": v(60.45, 32) * mm});
            skLineSegment(sketch, "E33.6.5.3", {"start": v(68.1, 32) * mm, "end": v(65.2, 37.02) * mm});
            skLineSegment(sketch, "E33.6.5.4", {"start": v(71, 37.02) * mm, "end": v(68.1, 32) * mm});
            skLineSegment(sketch, "E33.6.5.5", {"start": v(65.2, 37.02) * mm, "end": v(71, 37.02) * mm});
            skLineSegment(sketch, "E33.6.6.0", {"start": v(60.45, 38.4) * mm, "end": v(66.25, 38.4) * mm});
            skLineSegment(sketch, "E33.6.6.1", {"start": v(66.25, 38.4) * mm, "end": v(63.35, 43.42) * mm});
            skLineSegment(sketch, "E33.6.6.2", {"start": v(63.35, 43.42) * mm, "end": v(60.45, 38.4) * mm});
            skLineSegment(sketch, "E33.6.6.3", {"start": v(68.1, 38.4) * mm, "end": v(65.2, 43.42) * mm});
            skLineSegment(sketch, "E33.6.6.4", {"start": v(71, 43.42) * mm, "end": v(68.1, 38.4) * mm});
            skLineSegment(sketch, "E33.6.6.5", {"start": v(65.2, 43.42) * mm, "end": v(71, 43.42) * mm});
            skLineSegment(sketch, "E33.6.7.0", {"start": v(60.45, 44.8) * mm, "end": v(66.25, 44.8) * mm});
            skLineSegment(sketch, "E33.6.7.1", {"start": v(66.25, 44.8) * mm, "end": v(63.35, 49.82) * mm});
            skLineSegment(sketch, "E33.6.7.2", {"start": v(63.35, 49.82) * mm, "end": v(60.45, 44.8) * mm});
            skLineSegment(sketch, "E33.6.7.3", {"start": v(68.1, 44.8) * mm, "end": v(65.2, 49.82) * mm});
            skLineSegment(sketch, "E33.6.7.4", {"start": v(71, 49.82) * mm, "end": v(68.1, 44.8) * mm});
            skLineSegment(sketch, "E33.6.7.5", {"start": v(65.2, 49.82) * mm, "end": v(71, 49.82) * mm});
            skLineSegment(sketch, "E33.6.8.0", {"start": v(60.45, 51.2) * mm, "end": v(66.25, 51.2) * mm});
            skLineSegment(sketch, "E33.6.8.1", {"start": v(66.25, 51.2) * mm, "end": v(63.35, 56.22) * mm});
            skLineSegment(sketch, "E33.6.8.2", {"start": v(63.35, 56.22) * mm, "end": v(60.45, 51.2) * mm});
            skLineSegment(sketch, "E33.6.8.3", {"start": v(68.1, 51.2) * mm, "end": v(65.2, 56.22) * mm});
            skLineSegment(sketch, "E33.6.8.4", {"start": v(71, 56.22) * mm, "end": v(68.1, 51.2) * mm});
            skLineSegment(sketch, "E33.6.8.5", {"start": v(65.2, 56.22) * mm, "end": v(71, 56.22) * mm});
            skLineSegment(sketch, "E33.6.9.0", {"start": v(60.45, 57.6) * mm, "end": v(66.25, 57.6) * mm});
            skLineSegment(sketch, "E33.6.9.1", {"start": v(66.25, 57.6) * mm, "end": v(63.35, 62.62) * mm});
            skLineSegment(sketch, "E33.6.9.2", {"start": v(63.35, 62.62) * mm, "end": v(60.45, 57.6) * mm});
            skLineSegment(sketch, "E33.6.9.3", {"start": v(68.1, 57.6) * mm, "end": v(65.2, 62.62) * mm});
            skLineSegment(sketch, "E33.6.9.4", {"start": v(71, 62.62) * mm, "end": v(68.1, 57.6) * mm});
            skLineSegment(sketch, "E33.6.9.5", {"start": v(65.2, 62.62) * mm, "end": v(71, 62.62) * mm});
            skLineSegment(sketch, "E33.7.0.0", {"start": v(70.05, 0) * mm, "end": v(75.85, 0) * mm});
            skLineSegment(sketch, "E33.7.0.1", {"start": v(75.85, 0) * mm, "end": v(72.95, 5.02) * mm});
            skLineSegment(sketch, "E33.7.0.2", {"start": v(72.95, 5.02) * mm, "end": v(70.05, 0) * mm});
            skLineSegment(sketch, "E33.7.0.3", {"start": v(77.7, 0) * mm, "end": v(74.8, 5.02) * mm});
            skLineSegment(sketch, "E33.7.0.4", {"start": v(80.6, 5.02) * mm, "end": v(77.7, 0) * mm});
            skLineSegment(sketch, "E33.7.0.5", {"start": v(74.8, 5.02) * mm, "end": v(80.6, 5.02) * mm});
            skLineSegment(sketch, "E33.7.1.0", {"start": v(70.05, 6.4) * mm, "end": v(75.85, 6.4) * mm});
            skLineSegment(sketch, "E33.7.1.1", {"start": v(75.85, 6.4) * mm, "end": v(72.95, 11.42) * mm});
            skLineSegment(sketch, "E33.7.1.2", {"start": v(72.95, 11.42) * mm, "end": v(70.05, 6.4) * mm});
            skLineSegment(sketch, "E33.7.1.3", {"start": v(77.7, 6.4) * mm, "end": v(74.8, 11.42) * mm});
            skLineSegment(sketch, "E33.7.1.4", {"start": v(80.6, 11.42) * mm, "end": v(77.7, 6.4) * mm});
            skLineSegment(sketch, "E33.7.1.5", {"start": v(74.8, 11.42) * mm, "end": v(80.6, 11.42) * mm});
            skLineSegment(sketch, "E33.7.2.0", {"start": v(70.05, 12.8) * mm, "end": v(75.85, 12.8) * mm});
            skLineSegment(sketch, "E33.7.2.1", {"start": v(75.85, 12.8) * mm, "end": v(72.95, 17.82) * mm});
            skLineSegment(sketch, "E33.7.2.2", {"start": v(72.95, 17.82) * mm, "end": v(70.05, 12.8) * mm});
            skLineSegment(sketch, "E33.7.2.3", {"start": v(77.7, 12.8) * mm, "end": v(74.8, 17.82) * mm});
            skLineSegment(sketch, "E33.7.2.4", {"start": v(80.6, 17.82) * mm, "end": v(77.7, 12.8) * mm});
            skLineSegment(sketch, "E33.7.2.5", {"start": v(74.8, 17.82) * mm, "end": v(80.6, 17.82) * mm});
            skLineSegment(sketch, "E33.7.3.0", {"start": v(70.05, 19.2) * mm, "end": v(75.85, 19.2) * mm});
            skLineSegment(sketch, "E33.7.3.1", {"start": v(75.85, 19.2) * mm, "end": v(72.95, 24.22) * mm});
            skLineSegment(sketch, "E33.7.3.2", {"start": v(72.95, 24.22) * mm, "end": v(70.05, 19.2) * mm});
            skLineSegment(sketch, "E33.7.3.3", {"start": v(77.7, 19.2) * mm, "end": v(74.8, 24.22) * mm});
            skLineSegment(sketch, "E33.7.3.4", {"start": v(80.6, 24.22) * mm, "end": v(77.7, 19.2) * mm});
            skLineSegment(sketch, "E33.7.3.5", {"start": v(74.8, 24.22) * mm, "end": v(80.6, 24.22) * mm});
            skLineSegment(sketch, "E33.7.4.0", {"start": v(70.05, 25.6) * mm, "end": v(75.85, 25.6) * mm});
            skLineSegment(sketch, "E33.7.4.1", {"start": v(75.85, 25.6) * mm, "end": v(72.95, 30.62) * mm});
            skLineSegment(sketch, "E33.7.4.2", {"start": v(72.95, 30.62) * mm, "end": v(70.05, 25.6) * mm});
            skLineSegment(sketch, "E33.7.4.3", {"start": v(77.7, 25.6) * mm, "end": v(74.8, 30.62) * mm});
            skLineSegment(sketch, "E33.7.4.4", {"start": v(80.6, 30.62) * mm, "end": v(77.7, 25.6) * mm});
            skLineSegment(sketch, "E33.7.4.5", {"start": v(74.8, 30.62) * mm, "end": v(80.6, 30.62) * mm});
            skLineSegment(sketch, "E33.7.5.0", {"start": v(70.05, 32) * mm, "end": v(75.85, 32) * mm});
            skLineSegment(sketch, "E33.7.5.1", {"start": v(75.85, 32) * mm, "end": v(72.95, 37.02) * mm});
            skLineSegment(sketch, "E33.7.5.2", {"start": v(72.95, 37.02) * mm, "end": v(70.05, 32) * mm});
            skLineSegment(sketch, "E33.7.5.3", {"start": v(77.7, 32) * mm, "end": v(74.8, 37.02) * mm});
            skLineSegment(sketch, "E33.7.5.4", {"start": v(80.6, 37.02) * mm, "end": v(77.7, 32) * mm});
            skLineSegment(sketch, "E33.7.5.5", {"start": v(74.8, 37.02) * mm, "end": v(80.6, 37.02) * mm});
            skLineSegment(sketch, "E33.7.6.0", {"start": v(70.05, 38.4) * mm, "end": v(75.85, 38.4) * mm});
            skLineSegment(sketch, "E33.7.6.1", {"start": v(75.85, 38.4) * mm, "end": v(72.95, 43.42) * mm});
            skLineSegment(sketch, "E33.7.6.2", {"start": v(72.95, 43.42) * mm, "end": v(70.05, 38.4) * mm});
            skLineSegment(sketch, "E33.7.6.3", {"start": v(77.7, 38.4) * mm, "end": v(74.8, 43.42) * mm});
            skLineSegment(sketch, "E33.7.6.4", {"start": v(80.6, 43.42) * mm, "end": v(77.7, 38.4) * mm});
            skLineSegment(sketch, "E33.7.6.5", {"start": v(74.8, 43.42) * mm, "end": v(80.6, 43.42) * mm});
            skLineSegment(sketch, "E33.7.7.0", {"start": v(70.05, 44.8) * mm, "end": v(75.85, 44.8) * mm});
            skLineSegment(sketch, "E33.7.7.1", {"start": v(75.85, 44.8) * mm, "end": v(72.95, 49.82) * mm});
            skLineSegment(sketch, "E33.7.7.2", {"start": v(72.95, 49.82) * mm, "end": v(70.05, 44.8) * mm});
            skLineSegment(sketch, "E33.7.7.3", {"start": v(77.7, 44.8) * mm, "end": v(74.8, 49.82) * mm});
            skLineSegment(sketch, "E33.7.7.4", {"start": v(80.6, 49.82) * mm, "end": v(77.7, 44.8) * mm});
            skLineSegment(sketch, "E33.7.7.5", {"start": v(74.8, 49.82) * mm, "end": v(80.6, 49.82) * mm});
            skLineSegment(sketch, "E33.7.8.0", {"start": v(70.05, 51.2) * mm, "end": v(75.85, 51.2) * mm});
            skLineSegment(sketch, "E33.7.8.1", {"start": v(75.85, 51.2) * mm, "end": v(72.95, 56.22) * mm});
            skLineSegment(sketch, "E33.7.8.2", {"start": v(72.95, 56.22) * mm, "end": v(70.05, 51.2) * mm});
            skLineSegment(sketch, "E33.7.8.3", {"start": v(77.7, 51.2) * mm, "end": v(74.8, 56.22) * mm});
            skLineSegment(sketch, "E33.7.8.4", {"start": v(80.6, 56.22) * mm, "end": v(77.7, 51.2) * mm});
            skLineSegment(sketch, "E33.7.8.5", {"start": v(74.8, 56.22) * mm, "end": v(80.6, 56.22) * mm});
            skLineSegment(sketch, "E33.7.9.0", {"start": v(70.05, 57.6) * mm, "end": v(75.85, 57.6) * mm});
            skLineSegment(sketch, "E33.7.9.1", {"start": v(75.85, 57.6) * mm, "end": v(72.95, 62.62) * mm});
            skLineSegment(sketch, "E33.7.9.2", {"start": v(72.95, 62.62) * mm, "end": v(70.05, 57.6) * mm});
            skLineSegment(sketch, "E33.7.9.3", {"start": v(77.7, 57.6) * mm, "end": v(74.8, 62.62) * mm});
            skLineSegment(sketch, "E33.7.9.4", {"start": v(80.6, 62.62) * mm, "end": v(77.7, 57.6) * mm});
            skLineSegment(sketch, "E33.7.9.5", {"start": v(74.8, 62.62) * mm, "end": v(80.6, 62.62) * mm});
            skLineSegment(sketch, "E33.8.0.0", {"start": v(79.65, 0) * mm, "end": v(85.45, 0) * mm});
            skLineSegment(sketch, "E33.8.0.1", {"start": v(85.45, 0) * mm, "end": v(82.55, 5.02) * mm});
            skLineSegment(sketch, "E33.8.0.2", {"start": v(82.55, 5.02) * mm, "end": v(79.65, 0) * mm});
            skLineSegment(sketch, "E33.8.0.3", {"start": v(87.3, 0) * mm, "end": v(84.4, 5.02) * mm});
            skLineSegment(sketch, "E33.8.0.4", {"start": v(90.2, 5.02) * mm, "end": v(87.3, 0) * mm});
            skLineSegment(sketch, "E33.8.0.5", {"start": v(84.4, 5.02) * mm, "end": v(90.2, 5.02) * mm});
            skLineSegment(sketch, "E33.8.1.0", {"start": v(79.65, 6.4) * mm, "end": v(85.45, 6.4) * mm});
            skLineSegment(sketch, "E33.8.1.1", {"start": v(85.45, 6.4) * mm, "end": v(82.55, 11.42) * mm});
            skLineSegment(sketch, "E33.8.1.2", {"start": v(82.55, 11.42) * mm, "end": v(79.65, 6.4) * mm});
            skLineSegment(sketch, "E33.8.1.3", {"start": v(87.3, 6.4) * mm, "end": v(84.4, 11.42) * mm});
            skLineSegment(sketch, "E33.8.1.4", {"start": v(90.2, 11.42) * mm, "end": v(87.3, 6.4) * mm});
            skLineSegment(sketch, "E33.8.1.5", {"start": v(84.4, 11.42) * mm, "end": v(90.2, 11.42) * mm});
            skLineSegment(sketch, "E33.8.2.0", {"start": v(79.65, 12.8) * mm, "end": v(85.45, 12.8) * mm});
            skLineSegment(sketch, "E33.8.2.1", {"start": v(85.45, 12.8) * mm, "end": v(82.55, 17.82) * mm});
            skLineSegment(sketch, "E33.8.2.2", {"start": v(82.55, 17.82) * mm, "end": v(79.65, 12.8) * mm});
            skLineSegment(sketch, "E33.8.2.3", {"start": v(87.3, 12.8) * mm, "end": v(84.4, 17.82) * mm});
            skLineSegment(sketch, "E33.8.2.4", {"start": v(90.2, 17.82) * mm, "end": v(87.3, 12.8) * mm});
            skLineSegment(sketch, "E33.8.2.5", {"start": v(84.4, 17.82) * mm, "end": v(90.2, 17.82) * mm});
            skLineSegment(sketch, "E33.8.3.0", {"start": v(79.65, 19.2) * mm, "end": v(85.45, 19.2) * mm});
            skLineSegment(sketch, "E33.8.3.1", {"start": v(85.45, 19.2) * mm, "end": v(82.55, 24.22) * mm});
            skLineSegment(sketch, "E33.8.3.2", {"start": v(82.55, 24.22) * mm, "end": v(79.65, 19.2) * mm});
            skLineSegment(sketch, "E33.8.3.3", {"start": v(87.3, 19.2) * mm, "end": v(84.4, 24.22) * mm});
            skLineSegment(sketch, "E33.8.3.4", {"start": v(90.2, 24.22) * mm, "end": v(87.3, 19.2) * mm});
            skLineSegment(sketch, "E33.8.3.5", {"start": v(84.4, 24.22) * mm, "end": v(90.2, 24.22) * mm});
            skLineSegment(sketch, "E33.8.4.0", {"start": v(79.65, 25.6) * mm, "end": v(85.45, 25.6) * mm});
            skLineSegment(sketch, "E33.8.4.1", {"start": v(85.45, 25.6) * mm, "end": v(82.55, 30.62) * mm});
            skLineSegment(sketch, "E33.8.4.2", {"start": v(82.55, 30.62) * mm, "end": v(79.65, 25.6) * mm});
            skLineSegment(sketch, "E33.8.4.3", {"start": v(87.3, 25.6) * mm, "end": v(84.4, 30.62) * mm});
            skLineSegment(sketch, "E33.8.4.4", {"start": v(90.2, 30.62) * mm, "end": v(87.3, 25.6) * mm});
            skLineSegment(sketch, "E33.8.4.5", {"start": v(84.4, 30.62) * mm, "end": v(90.2, 30.62) * mm});
            skLineSegment(sketch, "E33.8.5.0", {"start": v(79.65, 32) * mm, "end": v(85.45, 32) * mm});
            skLineSegment(sketch, "E33.8.5.1", {"start": v(85.45, 32) * mm, "end": v(82.55, 37.02) * mm});
            skLineSegment(sketch, "E33.8.5.2", {"start": v(82.55, 37.02) * mm, "end": v(79.65, 32) * mm});
            skLineSegment(sketch, "E33.8.5.3", {"start": v(87.3, 32) * mm, "end": v(84.4, 37.02) * mm});
            skLineSegment(sketch, "E33.8.5.4", {"start": v(90.2, 37.02) * mm, "end": v(87.3, 32) * mm});
            skLineSegment(sketch, "E33.8.5.5", {"start": v(84.4, 37.02) * mm, "end": v(90.2, 37.02) * mm});
            skLineSegment(sketch, "E33.8.6.0", {"start": v(79.65, 38.4) * mm, "end": v(85.45, 38.4) * mm});
            skLineSegment(sketch, "E33.8.6.1", {"start": v(85.45, 38.4) * mm, "end": v(82.55, 43.42) * mm});
            skLineSegment(sketch, "E33.8.6.2", {"start": v(82.55, 43.42) * mm, "end": v(79.65, 38.4) * mm});
            skLineSegment(sketch, "E33.8.6.3", {"start": v(87.3, 38.4) * mm, "end": v(84.4, 43.42) * mm});
            skLineSegment(sketch, "E33.8.6.4", {"start": v(90.2, 43.42) * mm, "end": v(87.3, 38.4) * mm});
            skLineSegment(sketch, "E33.8.6.5", {"start": v(84.4, 43.42) * mm, "end": v(90.2, 43.42) * mm});
            skLineSegment(sketch, "E33.8.7.0", {"start": v(79.65, 44.8) * mm, "end": v(85.45, 44.8) * mm});
            skLineSegment(sketch, "E33.8.7.1", {"start": v(85.45, 44.8) * mm, "end": v(82.55, 49.82) * mm});
            skLineSegment(sketch, "E33.8.7.2", {"start": v(82.55, 49.82) * mm, "end": v(79.65, 44.8) * mm});
            skLineSegment(sketch, "E33.8.7.3", {"start": v(87.3, 44.8) * mm, "end": v(84.4, 49.82) * mm});
            skLineSegment(sketch, "E33.8.7.4", {"start": v(90.2, 49.82) * mm, "end": v(87.3, 44.8) * mm});
            skLineSegment(sketch, "E33.8.7.5", {"start": v(84.4, 49.82) * mm, "end": v(90.2, 49.82) * mm});
            skLineSegment(sketch, "E33.8.8.0", {"start": v(79.65, 51.2) * mm, "end": v(85.45, 51.2) * mm});
            skLineSegment(sketch, "E33.8.8.1", {"start": v(85.45, 51.2) * mm, "end": v(82.55, 56.22) * mm});
            skLineSegment(sketch, "E33.8.8.2", {"start": v(82.55, 56.22) * mm, "end": v(79.65, 51.2) * mm});
            skLineSegment(sketch, "E33.8.8.3", {"start": v(87.3, 51.2) * mm, "end": v(84.4, 56.22) * mm});
            skLineSegment(sketch, "E33.8.8.4", {"start": v(90.2, 56.22) * mm, "end": v(87.3, 51.2) * mm});
            skLineSegment(sketch, "E33.8.8.5", {"start": v(84.4, 56.22) * mm, "end": v(90.2, 56.22) * mm});
            skLineSegment(sketch, "E33.8.9.0", {"start": v(79.65, 57.6) * mm, "end": v(85.45, 57.6) * mm});
            skLineSegment(sketch, "E33.8.9.1", {"start": v(85.45, 57.6) * mm, "end": v(82.55, 62.62) * mm});
            skLineSegment(sketch, "E33.8.9.2", {"start": v(82.55, 62.62) * mm, "end": v(79.65, 57.6) * mm});
            skLineSegment(sketch, "E33.8.9.3", {"start": v(87.3, 57.6) * mm, "end": v(84.4, 62.62) * mm});
            skLineSegment(sketch, "E33.8.9.4", {"start": v(90.2, 62.62) * mm, "end": v(87.3, 57.6) * mm});
            skLineSegment(sketch, "E33.8.9.5", {"start": v(84.4, 62.62) * mm, "end": v(90.2, 62.62) * mm});
            skLineSegment(sketch, "E33.9.0.0", {"start": v(89.25, 0) * mm, "end": v(95.05, 0) * mm});
            skLineSegment(sketch, "E33.9.0.1", {"start": v(95.05, 0) * mm, "end": v(92.15, 5.02) * mm});
            skLineSegment(sketch, "E33.9.0.2", {"start": v(92.15, 5.02) * mm, "end": v(89.25, 0) * mm});
            skLineSegment(sketch, "E33.9.0.3", {"start": v(96.9, 0) * mm, "end": v(94, 5.02) * mm});
            skLineSegment(sketch, "E33.9.0.4", {"start": v(99.8, 5.02) * mm, "end": v(96.9, 0) * mm});
            skLineSegment(sketch, "E33.9.0.5", {"start": v(94, 5.02) * mm, "end": v(99.8, 5.02) * mm});
            skLineSegment(sketch, "E33.9.1.0", {"start": v(89.25, 6.4) * mm, "end": v(95.05, 6.4) * mm});
            skLineSegment(sketch, "E33.9.1.1", {"start": v(95.05, 6.4) * mm, "end": v(92.15, 11.42) * mm});
            skLineSegment(sketch, "E33.9.1.2", {"start": v(92.15, 11.42) * mm, "end": v(89.25, 6.4) * mm});
            skLineSegment(sketch, "E33.9.1.3", {"start": v(96.9, 6.4) * mm, "end": v(94, 11.42) * mm});
            skLineSegment(sketch, "E33.9.1.4", {"start": v(99.8, 11.42) * mm, "end": v(96.9, 6.4) * mm});
            skLineSegment(sketch, "E33.9.1.5", {"start": v(94, 11.42) * mm, "end": v(99.8, 11.42) * mm});
            skLineSegment(sketch, "E33.9.2.0", {"start": v(89.25, 12.8) * mm, "end": v(95.05, 12.8) * mm});
            skLineSegment(sketch, "E33.9.2.1", {"start": v(95.05, 12.8) * mm, "end": v(92.15, 17.82) * mm});
            skLineSegment(sketch, "E33.9.2.2", {"start": v(92.15, 17.82) * mm, "end": v(89.25, 12.8) * mm});
            skLineSegment(sketch, "E33.9.2.3", {"start": v(96.9, 12.8) * mm, "end": v(94, 17.82) * mm});
            skLineSegment(sketch, "E33.9.2.4", {"start": v(99.8, 17.82) * mm, "end": v(96.9, 12.8) * mm});
            skLineSegment(sketch, "E33.9.2.5", {"start": v(94, 17.82) * mm, "end": v(99.8, 17.82) * mm});
            skLineSegment(sketch, "E33.9.3.0", {"start": v(89.25, 19.2) * mm, "end": v(95.05, 19.2) * mm});
            skLineSegment(sketch, "E33.9.3.1", {"start": v(95.05, 19.2) * mm, "end": v(92.15, 24.22) * mm});
            skLineSegment(sketch, "E33.9.3.2", {"start": v(92.15, 24.22) * mm, "end": v(89.25, 19.2) * mm});
            skLineSegment(sketch, "E33.9.3.3", {"start": v(96.9, 19.2) * mm, "end": v(94, 24.22) * mm});
            skLineSegment(sketch, "E33.9.3.4", {"start": v(99.8, 24.22) * mm, "end": v(96.9, 19.2) * mm});
            skLineSegment(sketch, "E33.9.3.5", {"start": v(94, 24.22) * mm, "end": v(99.8, 24.22) * mm});
            skLineSegment(sketch, "E33.9.4.0", {"start": v(89.25, 25.6) * mm, "end": v(95.05, 25.6) * mm});
            skLineSegment(sketch, "E33.9.4.1", {"start": v(95.05, 25.6) * mm, "end": v(92.15, 30.62) * mm});
            skLineSegment(sketch, "E33.9.4.2", {"start": v(92.15, 30.62) * mm, "end": v(89.25, 25.6) * mm});
            skLineSegment(sketch, "E33.9.4.3", {"start": v(96.9, 25.6) * mm, "end": v(94, 30.62) * mm});
            skLineSegment(sketch, "E33.9.4.4", {"start": v(99.8, 30.62) * mm, "end": v(96.9, 25.6) * mm});
            skLineSegment(sketch, "E33.9.4.5", {"start": v(94, 30.62) * mm, "end": v(99.8, 30.62) * mm});
            skLineSegment(sketch, "E33.9.5.0", {"start": v(89.25, 32) * mm, "end": v(95.05, 32) * mm});
            skLineSegment(sketch, "E33.9.5.1", {"start": v(95.05, 32) * mm, "end": v(92.15, 37.02) * mm});
            skLineSegment(sketch, "E33.9.5.2", {"start": v(92.15, 37.02) * mm, "end": v(89.25, 32) * mm});
            skLineSegment(sketch, "E33.9.5.3", {"start": v(96.9, 32) * mm, "end": v(94, 37.02) * mm});
            skLineSegment(sketch, "E33.9.5.4", {"start": v(99.8, 37.02) * mm, "end": v(96.9, 32) * mm});
            skLineSegment(sketch, "E33.9.5.5", {"start": v(94, 37.02) * mm, "end": v(99.8, 37.02) * mm});
            skLineSegment(sketch, "E33.9.6.0", {"start": v(89.25, 38.4) * mm, "end": v(95.05, 38.4) * mm});
            skLineSegment(sketch, "E33.9.6.1", {"start": v(95.05, 38.4) * mm, "end": v(92.15, 43.42) * mm});
            skLineSegment(sketch, "E33.9.6.2", {"start": v(92.15, 43.42) * mm, "end": v(89.25, 38.4) * mm});
            skLineSegment(sketch, "E33.9.6.3", {"start": v(96.9, 38.4) * mm, "end": v(94, 43.42) * mm});
            skLineSegment(sketch, "E33.9.6.4", {"start": v(99.8, 43.42) * mm, "end": v(96.9, 38.4) * mm});
            skLineSegment(sketch, "E33.9.6.5", {"start": v(94, 43.42) * mm, "end": v(99.8, 43.42) * mm});
            skLineSegment(sketch, "E33.9.7.0", {"start": v(89.25, 44.8) * mm, "end": v(95.05, 44.8) * mm});
            skLineSegment(sketch, "E33.9.7.1", {"start": v(95.05, 44.8) * mm, "end": v(92.15, 49.82) * mm});
            skLineSegment(sketch, "E33.9.7.2", {"start": v(92.15, 49.82) * mm, "end": v(89.25, 44.8) * mm});
            skLineSegment(sketch, "E33.9.7.3", {"start": v(96.9, 44.8) * mm, "end": v(94, 49.82) * mm});
            skLineSegment(sketch, "E33.9.7.4", {"start": v(99.8, 49.82) * mm, "end": v(96.9, 44.8) * mm});
            skLineSegment(sketch, "E33.9.7.5", {"start": v(94, 49.82) * mm, "end": v(99.8, 49.82) * mm});
            skLineSegment(sketch, "E33.9.8.0", {"start": v(89.25, 51.2) * mm, "end": v(95.05, 51.2) * mm});
            skLineSegment(sketch, "E33.9.8.1", {"start": v(95.05, 51.2) * mm, "end": v(92.15, 56.22) * mm});
            skLineSegment(sketch, "E33.9.8.2", {"start": v(92.15, 56.22) * mm, "end": v(89.25, 51.2) * mm});
            skLineSegment(sketch, "E33.9.8.3", {"start": v(96.9, 51.2) * mm, "end": v(94, 56.22) * mm});
            skLineSegment(sketch, "E33.9.8.4", {"start": v(99.8, 56.22) * mm, "end": v(96.9, 51.2) * mm});
            skLineSegment(sketch, "E33.9.8.5", {"start": v(94, 56.22) * mm, "end": v(99.8, 56.22) * mm});
            skLineSegment(sketch, "E33.9.9.0", {"start": v(89.25, 57.6) * mm, "end": v(95.05, 57.6) * mm});
            skLineSegment(sketch, "E33.9.9.1", {"start": v(95.05, 57.6) * mm, "end": v(92.15, 62.62) * mm});
            skLineSegment(sketch, "E33.9.9.2", {"start": v(92.15, 62.62) * mm, "end": v(89.25, 57.6) * mm});
            skLineSegment(sketch, "E33.9.9.3", {"start": v(96.9, 57.6) * mm, "end": v(94, 62.62) * mm});
            skLineSegment(sketch, "E33.9.9.4", {"start": v(99.8, 62.62) * mm, "end": v(96.9, 57.6) * mm});
            skLineSegment(sketch, "E33.9.9.5", {"start": v(94, 62.62) * mm, "end": v(99.8, 62.62) * mm});
            skLineSegment(sketch, "E33.10.0.0", {"start": v(98.85, 0) * mm, "end": v(104.65, 0) * mm});
            skLineSegment(sketch, "E33.10.0.1", {"start": v(104.65, 0) * mm, "end": v(101.75, 5.02) * mm});
            skLineSegment(sketch, "E33.10.0.2", {"start": v(101.75, 5.02) * mm, "end": v(98.85, 0) * mm});
            skLineSegment(sketch, "E33.10.0.3", {"start": v(106.5, 0) * mm, "end": v(103.6, 5.02) * mm});
            skLineSegment(sketch, "E33.10.0.4", {"start": v(109.4, 5.02) * mm, "end": v(106.5, 0) * mm});
            skLineSegment(sketch, "E33.10.0.5", {"start": v(103.6, 5.02) * mm, "end": v(109.4, 5.02) * mm});
            skLineSegment(sketch, "E33.10.1.0", {"start": v(98.85, 6.4) * mm, "end": v(104.65, 6.4) * mm});
            skLineSegment(sketch, "E33.10.1.1", {"start": v(104.65, 6.4) * mm, "end": v(101.75, 11.42) * mm});
            skLineSegment(sketch, "E33.10.1.2", {"start": v(101.75, 11.42) * mm, "end": v(98.85, 6.4) * mm});
            skLineSegment(sketch, "E33.10.1.3", {"start": v(106.5, 6.4) * mm, "end": v(103.6, 11.42) * mm});
            skLineSegment(sketch, "E33.10.1.4", {"start": v(109.4, 11.42) * mm, "end": v(106.5, 6.4) * mm});
            skLineSegment(sketch, "E33.10.1.5", {"start": v(103.6, 11.42) * mm, "end": v(109.4, 11.42) * mm});
            skLineSegment(sketch, "E33.10.2.0", {"start": v(98.85, 12.8) * mm, "end": v(104.65, 12.8) * mm});
            skLineSegment(sketch, "E33.10.2.1", {"start": v(104.65, 12.8) * mm, "end": v(101.75, 17.82) * mm});
            skLineSegment(sketch, "E33.10.2.2", {"start": v(101.75, 17.82) * mm, "end": v(98.85, 12.8) * mm});
            skLineSegment(sketch, "E33.10.2.3", {"start": v(106.5, 12.8) * mm, "end": v(103.6, 17.82) * mm});
            skLineSegment(sketch, "E33.10.2.4", {"start": v(109.4, 17.82) * mm, "end": v(106.5, 12.8) * mm});
            skLineSegment(sketch, "E33.10.2.5", {"start": v(103.6, 17.82) * mm, "end": v(109.4, 17.82) * mm});
            skLineSegment(sketch, "E33.10.3.0", {"start": v(98.85, 19.2) * mm, "end": v(104.65, 19.2) * mm});
            skLineSegment(sketch, "E33.10.3.1", {"start": v(104.65, 19.2) * mm, "end": v(101.75, 24.22) * mm});
            skLineSegment(sketch, "E33.10.3.2", {"start": v(101.75, 24.22) * mm, "end": v(98.85, 19.2) * mm});
            skLineSegment(sketch, "E33.10.3.3", {"start": v(106.5, 19.2) * mm, "end": v(103.6, 24.22) * mm});
            skLineSegment(sketch, "E33.10.3.4", {"start": v(109.4, 24.22) * mm, "end": v(106.5, 19.2) * mm});
            skLineSegment(sketch, "E33.10.3.5", {"start": v(103.6, 24.22) * mm, "end": v(109.4, 24.22) * mm});
            skLineSegment(sketch, "E33.10.4.0", {"start": v(98.85, 25.6) * mm, "end": v(104.65, 25.6) * mm});
            skLineSegment(sketch, "E33.10.4.1", {"start": v(104.65, 25.6) * mm, "end": v(101.75, 30.62) * mm});
            skLineSegment(sketch, "E33.10.4.2", {"start": v(101.75, 30.62) * mm, "end": v(98.85, 25.6) * mm});
            skLineSegment(sketch, "E33.10.4.3", {"start": v(106.5, 25.6) * mm, "end": v(103.6, 30.62) * mm});
            skLineSegment(sketch, "E33.10.4.4", {"start": v(109.4, 30.62) * mm, "end": v(106.5, 25.6) * mm});
            skLineSegment(sketch, "E33.10.4.5", {"start": v(103.6, 30.62) * mm, "end": v(109.4, 30.62) * mm});
            skLineSegment(sketch, "E33.10.5.0", {"start": v(98.85, 32) * mm, "end": v(104.65, 32) * mm});
            skLineSegment(sketch, "E33.10.5.1", {"start": v(104.65, 32) * mm, "end": v(101.75, 37.02) * mm});
            skLineSegment(sketch, "E33.10.5.2", {"start": v(101.75, 37.02) * mm, "end": v(98.85, 32) * mm});
            skLineSegment(sketch, "E33.10.5.3", {"start": v(106.5, 32) * mm, "end": v(103.6, 37.02) * mm});
            skLineSegment(sketch, "E33.10.5.4", {"start": v(109.4, 37.02) * mm, "end": v(106.5, 32) * mm});
            skLineSegment(sketch, "E33.10.5.5", {"start": v(103.6, 37.02) * mm, "end": v(109.4, 37.02) * mm});
            skLineSegment(sketch, "E33.10.6.0", {"start": v(98.85, 38.4) * mm, "end": v(104.65, 38.4) * mm});
            skLineSegment(sketch, "E33.10.6.1", {"start": v(104.65, 38.4) * mm, "end": v(101.75, 43.42) * mm});
            skLineSegment(sketch, "E33.10.6.2", {"start": v(101.75, 43.42) * mm, "end": v(98.85, 38.4) * mm});
            skLineSegment(sketch, "E33.10.6.3", {"start": v(106.5, 38.4) * mm, "end": v(103.6, 43.42) * mm});
            skLineSegment(sketch, "E33.10.6.4", {"start": v(109.4, 43.42) * mm, "end": v(106.5, 38.4) * mm});
            skLineSegment(sketch, "E33.10.6.5", {"start": v(103.6, 43.42) * mm, "end": v(109.4, 43.42) * mm});
            skLineSegment(sketch, "E33.10.7.0", {"start": v(98.85, 44.8) * mm, "end": v(104.65, 44.8) * mm});
            skLineSegment(sketch, "E33.10.7.1", {"start": v(104.65, 44.8) * mm, "end": v(101.75, 49.82) * mm});
            skLineSegment(sketch, "E33.10.7.2", {"start": v(101.75, 49.82) * mm, "end": v(98.85, 44.8) * mm});
            skLineSegment(sketch, "E33.10.7.3", {"start": v(106.5, 44.8) * mm, "end": v(103.6, 49.82) * mm});
            skLineSegment(sketch, "E33.10.7.4", {"start": v(109.4, 49.82) * mm, "end": v(106.5, 44.8) * mm});
            skLineSegment(sketch, "E33.10.7.5", {"start": v(103.6, 49.82) * mm, "end": v(109.4, 49.82) * mm});
            skLineSegment(sketch, "E33.10.8.0", {"start": v(98.85, 51.2) * mm, "end": v(104.65, 51.2) * mm});
            skLineSegment(sketch, "E33.10.8.1", {"start": v(104.65, 51.2) * mm, "end": v(101.75, 56.22) * mm});
            skLineSegment(sketch, "E33.10.8.2", {"start": v(101.75, 56.22) * mm, "end": v(98.85, 51.2) * mm});
            skLineSegment(sketch, "E33.10.8.3", {"start": v(106.5, 51.2) * mm, "end": v(103.6, 56.22) * mm});
            skLineSegment(sketch, "E33.10.8.4", {"start": v(109.4, 56.22) * mm, "end": v(106.5, 51.2) * mm});
            skLineSegment(sketch, "E33.10.8.5", {"start": v(103.6, 56.22) * mm, "end": v(109.4, 56.22) * mm});
            skLineSegment(sketch, "E33.10.9.0", {"start": v(98.85, 57.6) * mm, "end": v(104.65, 57.6) * mm});
            skLineSegment(sketch, "E33.10.9.1", {"start": v(104.65, 57.6) * mm, "end": v(101.75, 62.62) * mm});
            skLineSegment(sketch, "E33.10.9.2", {"start": v(101.75, 62.62) * mm, "end": v(98.85, 57.6) * mm});
            skLineSegment(sketch, "E33.10.9.3", {"start": v(106.5, 57.6) * mm, "end": v(103.6, 62.62) * mm});
            skLineSegment(sketch, "E33.10.9.4", {"start": v(109.4, 62.62) * mm, "end": v(106.5, 57.6) * mm});
            skLineSegment(sketch, "E33.10.9.5", {"start": v(103.6, 62.62) * mm, "end": v(109.4, 62.62) * mm});
            skLineSegment(sketch, "E33.11.0.0", {"start": v(108.45, 0) * mm, "end": v(114.25, 0) * mm});
            skLineSegment(sketch, "E33.11.0.1", {"start": v(114.25, 0) * mm, "end": v(111.35, 5.02) * mm});
            skLineSegment(sketch, "E33.11.0.2", {"start": v(111.35, 5.02) * mm, "end": v(108.45, 0) * mm});
            skLineSegment(sketch, "E33.11.0.3", {"start": v(116.1, 0) * mm, "end": v(113.2, 5.02) * mm});
            skLineSegment(sketch, "E33.11.0.4", {"start": v(119, 5.02) * mm, "end": v(116.1, 0) * mm});
            skLineSegment(sketch, "E33.11.0.5", {"start": v(113.2, 5.02) * mm, "end": v(119, 5.02) * mm});
            skLineSegment(sketch, "E33.11.1.0", {"start": v(108.45, 6.4) * mm, "end": v(114.25, 6.4) * mm});
            skLineSegment(sketch, "E33.11.1.1", {"start": v(114.25, 6.4) * mm, "end": v(111.35, 11.42) * mm});
            skLineSegment(sketch, "E33.11.1.2", {"start": v(111.35, 11.42) * mm, "end": v(108.45, 6.4) * mm});
            skLineSegment(sketch, "E33.11.1.3", {"start": v(116.1, 6.4) * mm, "end": v(113.2, 11.42) * mm});
            skLineSegment(sketch, "E33.11.1.4", {"start": v(119, 11.42) * mm, "end": v(116.1, 6.4) * mm});
            skLineSegment(sketch, "E33.11.1.5", {"start": v(113.2, 11.42) * mm, "end": v(119, 11.42) * mm});
            skLineSegment(sketch, "E33.11.2.0", {"start": v(108.45, 12.8) * mm, "end": v(114.25, 12.8) * mm});
            skLineSegment(sketch, "E33.11.2.1", {"start": v(114.25, 12.8) * mm, "end": v(111.35, 17.82) * mm});
            skLineSegment(sketch, "E33.11.2.2", {"start": v(111.35, 17.82) * mm, "end": v(108.45, 12.8) * mm});
            skLineSegment(sketch, "E33.11.2.3", {"start": v(116.1, 12.8) * mm, "end": v(113.2, 17.82) * mm});
            skLineSegment(sketch, "E33.11.2.4", {"start": v(119, 17.82) * mm, "end": v(116.1, 12.8) * mm});
            skLineSegment(sketch, "E33.11.2.5", {"start": v(113.2, 17.82) * mm, "end": v(119, 17.82) * mm});
            skLineSegment(sketch, "E33.11.3.0", {"start": v(108.45, 19.2) * mm, "end": v(114.25, 19.2) * mm});
            skLineSegment(sketch, "E33.11.3.1", {"start": v(114.25, 19.2) * mm, "end": v(111.35, 24.22) * mm});
            skLineSegment(sketch, "E33.11.3.2", {"start": v(111.35, 24.22) * mm, "end": v(108.45, 19.2) * mm});
            skLineSegment(sketch, "E33.11.3.3", {"start": v(116.1, 19.2) * mm, "end": v(113.2, 24.22) * mm});
            skLineSegment(sketch, "E33.11.3.4", {"start": v(119, 24.22) * mm, "end": v(116.1, 19.2) * mm});
            skLineSegment(sketch, "E33.11.3.5", {"start": v(113.2, 24.22) * mm, "end": v(119, 24.22) * mm});
            skLineSegment(sketch, "E33.11.4.0", {"start": v(108.45, 25.6) * mm, "end": v(114.25, 25.6) * mm});
            skLineSegment(sketch, "E33.11.4.1", {"start": v(114.25, 25.6) * mm, "end": v(111.35, 30.62) * mm});
            skLineSegment(sketch, "E33.11.4.2", {"start": v(111.35, 30.62) * mm, "end": v(108.45, 25.6) * mm});
            skLineSegment(sketch, "E33.11.4.3", {"start": v(116.1, 25.6) * mm, "end": v(113.2, 30.62) * mm});
            skLineSegment(sketch, "E33.11.4.4", {"start": v(119, 30.62) * mm, "end": v(116.1, 25.6) * mm});
            skLineSegment(sketch, "E33.11.4.5", {"start": v(113.2, 30.62) * mm, "end": v(119, 30.62) * mm});
            skLineSegment(sketch, "E33.11.5.0", {"start": v(108.45, 32) * mm, "end": v(114.25, 32) * mm});
            skLineSegment(sketch, "E33.11.5.1", {"start": v(114.25, 32) * mm, "end": v(111.35, 37.02) * mm});
            skLineSegment(sketch, "E33.11.5.2", {"start": v(111.35, 37.02) * mm, "end": v(108.45, 32) * mm});
            skLineSegment(sketch, "E33.11.5.3", {"start": v(116.1, 32) * mm, "end": v(113.2, 37.02) * mm});
            skLineSegment(sketch, "E33.11.5.4", {"start": v(119, 37.02) * mm, "end": v(116.1, 32) * mm});
            skLineSegment(sketch, "E33.11.5.5", {"start": v(113.2, 37.02) * mm, "end": v(119, 37.02) * mm});
            skLineSegment(sketch, "E33.11.6.0", {"start": v(108.45, 38.4) * mm, "end": v(114.25, 38.4) * mm});
            skLineSegment(sketch, "E33.11.6.1", {"start": v(114.25, 38.4) * mm, "end": v(111.35, 43.42) * mm});
            skLineSegment(sketch, "E33.11.6.2", {"start": v(111.35, 43.42) * mm, "end": v(108.45, 38.4) * mm});
            skLineSegment(sketch, "E33.11.6.3", {"start": v(116.1, 38.4) * mm, "end": v(113.2, 43.42) * mm});
            skLineSegment(sketch, "E33.11.6.4", {"start": v(119, 43.42) * mm, "end": v(116.1, 38.4) * mm});
            skLineSegment(sketch, "E33.11.6.5", {"start": v(113.2, 43.42) * mm, "end": v(119, 43.42) * mm});
            skLineSegment(sketch, "E33.11.7.0", {"start": v(108.45, 44.8) * mm, "end": v(114.25, 44.8) * mm});
            skLineSegment(sketch, "E33.11.7.1", {"start": v(114.25, 44.8) * mm, "end": v(111.35, 49.82) * mm});
            skLineSegment(sketch, "E33.11.7.2", {"start": v(111.35, 49.82) * mm, "end": v(108.45, 44.8) * mm});
            skLineSegment(sketch, "E33.11.7.3", {"start": v(116.1, 44.8) * mm, "end": v(113.2, 49.82) * mm});
            skLineSegment(sketch, "E33.11.7.4", {"start": v(119, 49.82) * mm, "end": v(116.1, 44.8) * mm});
            skLineSegment(sketch, "E33.11.7.5", {"start": v(113.2, 49.82) * mm, "end": v(119, 49.82) * mm});
            skLineSegment(sketch, "E33.11.8.0", {"start": v(108.45, 51.2) * mm, "end": v(114.25, 51.2) * mm});
            skLineSegment(sketch, "E33.11.8.1", {"start": v(114.25, 51.2) * mm, "end": v(111.35, 56.22) * mm});
            skLineSegment(sketch, "E33.11.8.2", {"start": v(111.35, 56.22) * mm, "end": v(108.45, 51.2) * mm});
            skLineSegment(sketch, "E33.11.8.3", {"start": v(116.1, 51.2) * mm, "end": v(113.2, 56.22) * mm});
            skLineSegment(sketch, "E33.11.8.4", {"start": v(119, 56.22) * mm, "end": v(116.1, 51.2) * mm});
            skLineSegment(sketch, "E33.11.8.5", {"start": v(113.2, 56.22) * mm, "end": v(119, 56.22) * mm});
            skLineSegment(sketch, "E33.11.9.0", {"start": v(108.45, 57.6) * mm, "end": v(114.25, 57.6) * mm});
            skLineSegment(sketch, "E33.11.9.1", {"start": v(114.25, 57.6) * mm, "end": v(111.35, 62.62) * mm});
            skLineSegment(sketch, "E33.11.9.2", {"start": v(111.35, 62.62) * mm, "end": v(108.45, 57.6) * mm});
            skLineSegment(sketch, "E33.11.9.3", {"start": v(116.1, 57.6) * mm, "end": v(113.2, 62.62) * mm});
            skLineSegment(sketch, "E33.11.9.4", {"start": v(119, 62.62) * mm, "end": v(116.1, 57.6) * mm});
            skLineSegment(sketch, "E33.11.9.5", {"start": v(113.2, 62.62) * mm, "end": v(119, 62.62) * mm});
            skLineSegment(sketch, "E33.12.0.0", {"start": v(118.05, 0) * mm, "end": v(123.85, 0) * mm});
            skLineSegment(sketch, "E33.12.0.1", {"start": v(123.85, 0) * mm, "end": v(120.95, 5.02) * mm});
            skLineSegment(sketch, "E33.12.0.2", {"start": v(120.95, 5.02) * mm, "end": v(118.05, 0) * mm});
            skLineSegment(sketch, "E33.12.0.3", {"start": v(125.7, 0) * mm, "end": v(122.8, 5.02) * mm});
            skLineSegment(sketch, "E33.12.0.4", {"start": v(128.6, 5.02) * mm, "end": v(125.7, 0) * mm});
            skLineSegment(sketch, "E33.12.0.5", {"start": v(122.8, 5.02) * mm, "end": v(128.6, 5.02) * mm});
            skLineSegment(sketch, "E33.12.1.0", {"start": v(118.05, 6.4) * mm, "end": v(123.85, 6.4) * mm});
            skLineSegment(sketch, "E33.12.1.1", {"start": v(123.85, 6.4) * mm, "end": v(120.95, 11.42) * mm});
            skLineSegment(sketch, "E33.12.1.2", {"start": v(120.95, 11.42) * mm, "end": v(118.05, 6.4) * mm});
            skLineSegment(sketch, "E33.12.1.3", {"start": v(125.7, 6.4) * mm, "end": v(122.8, 11.42) * mm});
            skLineSegment(sketch, "E33.12.1.4", {"start": v(128.6, 11.42) * mm, "end": v(125.7, 6.4) * mm});
            skLineSegment(sketch, "E33.12.1.5", {"start": v(122.8, 11.42) * mm, "end": v(128.6, 11.42) * mm});
            skLineSegment(sketch, "E33.12.2.0", {"start": v(118.05, 12.8) * mm, "end": v(123.85, 12.8) * mm});
            skLineSegment(sketch, "E33.12.2.1", {"start": v(123.85, 12.8) * mm, "end": v(120.95, 17.82) * mm});
            skLineSegment(sketch, "E33.12.2.2", {"start": v(120.95, 17.82) * mm, "end": v(118.05, 12.8) * mm});
            skLineSegment(sketch, "E33.12.2.3", {"start": v(125.7, 12.8) * mm, "end": v(122.8, 17.82) * mm});
            skLineSegment(sketch, "E33.12.2.4", {"start": v(128.6, 17.82) * mm, "end": v(125.7, 12.8) * mm});
            skLineSegment(sketch, "E33.12.2.5", {"start": v(122.8, 17.82) * mm, "end": v(128.6, 17.82) * mm});
            skLineSegment(sketch, "E33.12.3.0", {"start": v(118.05, 19.2) * mm, "end": v(123.85, 19.2) * mm});
            skLineSegment(sketch, "E33.12.3.1", {"start": v(123.85, 19.2) * mm, "end": v(120.95, 24.22) * mm});
            skLineSegment(sketch, "E33.12.3.2", {"start": v(120.95, 24.22) * mm, "end": v(118.05, 19.2) * mm});
            skLineSegment(sketch, "E33.12.3.3", {"start": v(125.7, 19.2) * mm, "end": v(122.8, 24.22) * mm});
            skLineSegment(sketch, "E33.12.3.4", {"start": v(128.6, 24.22) * mm, "end": v(125.7, 19.2) * mm});
            skLineSegment(sketch, "E33.12.3.5", {"start": v(122.8, 24.22) * mm, "end": v(128.6, 24.22) * mm});
            skLineSegment(sketch, "E33.12.4.0", {"start": v(118.05, 25.6) * mm, "end": v(123.85, 25.6) * mm});
            skLineSegment(sketch, "E33.12.4.1", {"start": v(123.85, 25.6) * mm, "end": v(120.95, 30.62) * mm});
            skLineSegment(sketch, "E33.12.4.2", {"start": v(120.95, 30.62) * mm, "end": v(118.05, 25.6) * mm});
            skLineSegment(sketch, "E33.12.4.3", {"start": v(125.7, 25.6) * mm, "end": v(122.8, 30.62) * mm});
            skLineSegment(sketch, "E33.12.4.4", {"start": v(128.6, 30.62) * mm, "end": v(125.7, 25.6) * mm});
            skLineSegment(sketch, "E33.12.4.5", {"start": v(122.8, 30.62) * mm, "end": v(128.6, 30.62) * mm});
            skLineSegment(sketch, "E33.12.5.0", {"start": v(118.05, 32) * mm, "end": v(123.85, 32) * mm});
            skLineSegment(sketch, "E33.12.5.1", {"start": v(123.85, 32) * mm, "end": v(120.95, 37.02) * mm});
            skLineSegment(sketch, "E33.12.5.2", {"start": v(120.95, 37.02) * mm, "end": v(118.05, 32) * mm});
            skLineSegment(sketch, "E33.12.5.3", {"start": v(125.7, 32) * mm, "end": v(122.8, 37.02) * mm});
            skLineSegment(sketch, "E33.12.5.4", {"start": v(128.6, 37.02) * mm, "end": v(125.7, 32) * mm});
            skLineSegment(sketch, "E33.12.5.5", {"start": v(122.8, 37.02) * mm, "end": v(128.6, 37.02) * mm});
            skLineSegment(sketch, "E33.12.6.0", {"start": v(118.05, 38.4) * mm, "end": v(123.85, 38.4) * mm});
            skLineSegment(sketch, "E33.12.6.1", {"start": v(123.85, 38.4) * mm, "end": v(120.95, 43.42) * mm});
            skLineSegment(sketch, "E33.12.6.2", {"start": v(120.95, 43.42) * mm, "end": v(118.05, 38.4) * mm});
            skLineSegment(sketch, "E33.12.6.3", {"start": v(125.7, 38.4) * mm, "end": v(122.8, 43.42) * mm});
            skLineSegment(sketch, "E33.12.6.4", {"start": v(128.6, 43.42) * mm, "end": v(125.7, 38.4) * mm});
            skLineSegment(sketch, "E33.12.6.5", {"start": v(122.8, 43.42) * mm, "end": v(128.6, 43.42) * mm});
            skLineSegment(sketch, "E33.12.7.0", {"start": v(118.05, 44.8) * mm, "end": v(123.85, 44.8) * mm});
            skLineSegment(sketch, "E33.12.7.1", {"start": v(123.85, 44.8) * mm, "end": v(120.95, 49.82) * mm});
            skLineSegment(sketch, "E33.12.7.2", {"start": v(120.95, 49.82) * mm, "end": v(118.05, 44.8) * mm});
            skLineSegment(sketch, "E33.12.7.3", {"start": v(125.7, 44.8) * mm, "end": v(122.8, 49.82) * mm});
            skLineSegment(sketch, "E33.12.7.4", {"start": v(128.6, 49.82) * mm, "end": v(125.7, 44.8) * mm});
            skLineSegment(sketch, "E33.12.7.5", {"start": v(122.8, 49.82) * mm, "end": v(128.6, 49.82) * mm});
            skLineSegment(sketch, "E33.12.8.0", {"start": v(118.05, 51.2) * mm, "end": v(123.85, 51.2) * mm});
            skLineSegment(sketch, "E33.12.8.1", {"start": v(123.85, 51.2) * mm, "end": v(120.95, 56.22) * mm});
            skLineSegment(sketch, "E33.12.8.2", {"start": v(120.95, 56.22) * mm, "end": v(118.05, 51.2) * mm});
            skLineSegment(sketch, "E33.12.8.3", {"start": v(125.7, 51.2) * mm, "end": v(122.8, 56.22) * mm});
            skLineSegment(sketch, "E33.12.8.4", {"start": v(128.6, 56.22) * mm, "end": v(125.7, 51.2) * mm});
            skLineSegment(sketch, "E33.12.8.5", {"start": v(122.8, 56.22) * mm, "end": v(128.6, 56.22) * mm});
            skLineSegment(sketch, "E33.12.9.0", {"start": v(118.05, 57.6) * mm, "end": v(123.85, 57.6) * mm});
            skLineSegment(sketch, "E33.12.9.1", {"start": v(123.85, 57.6) * mm, "end": v(120.95, 62.62) * mm});
            skLineSegment(sketch, "E33.12.9.2", {"start": v(120.95, 62.62) * mm, "end": v(118.05, 57.6) * mm});
            skLineSegment(sketch, "E33.12.9.3", {"start": v(125.7, 57.6) * mm, "end": v(122.8, 62.62) * mm});
            skLineSegment(sketch, "E33.12.9.4", {"start": v(128.6, 62.62) * mm, "end": v(125.7, 57.6) * mm});
            skLineSegment(sketch, "E33.12.9.5", {"start": v(122.8, 62.62) * mm, "end": v(128.6, 62.62) * mm});
            skLineSegment(sketch, "E33.13.0.0", {"start": v(127.65, 0) * mm, "end": v(133.45, 0) * mm});
            skLineSegment(sketch, "E33.13.0.1", {"start": v(133.45, 0) * mm, "end": v(130.55, 5.02) * mm});
            skLineSegment(sketch, "E33.13.0.2", {"start": v(130.55, 5.02) * mm, "end": v(127.65, 0) * mm});
            skLineSegment(sketch, "E33.13.0.3", {"start": v(135.3, 0) * mm, "end": v(132.4, 5.02) * mm});
            skLineSegment(sketch, "E33.13.0.4", {"start": v(138.2, 5.02) * mm, "end": v(135.3, 0) * mm});
            skLineSegment(sketch, "E33.13.0.5", {"start": v(132.4, 5.02) * mm, "end": v(138.2, 5.02) * mm});
            skLineSegment(sketch, "E33.13.1.0", {"start": v(127.65, 6.4) * mm, "end": v(133.45, 6.4) * mm});
            skLineSegment(sketch, "E33.13.1.1", {"start": v(133.45, 6.4) * mm, "end": v(130.55, 11.42) * mm});
            skLineSegment(sketch, "E33.13.1.2", {"start": v(130.55, 11.42) * mm, "end": v(127.65, 6.4) * mm});
            skLineSegment(sketch, "E33.13.1.3", {"start": v(135.3, 6.4) * mm, "end": v(132.4, 11.42) * mm});
            skLineSegment(sketch, "E33.13.1.4", {"start": v(138.2, 11.42) * mm, "end": v(135.3, 6.4) * mm});
            skLineSegment(sketch, "E33.13.1.5", {"start": v(132.4, 11.42) * mm, "end": v(138.2, 11.42) * mm});
            skLineSegment(sketch, "E33.13.2.0", {"start": v(127.65, 12.8) * mm, "end": v(133.45, 12.8) * mm});
            skLineSegment(sketch, "E33.13.2.1", {"start": v(133.45, 12.8) * mm, "end": v(130.55, 17.82) * mm});
            skLineSegment(sketch, "E33.13.2.2", {"start": v(130.55, 17.82) * mm, "end": v(127.65, 12.8) * mm});
            skLineSegment(sketch, "E33.13.2.3", {"start": v(135.3, 12.8) * mm, "end": v(132.4, 17.82) * mm});
            skLineSegment(sketch, "E33.13.2.4", {"start": v(138.2, 17.82) * mm, "end": v(135.3, 12.8) * mm});
            skLineSegment(sketch, "E33.13.2.5", {"start": v(132.4, 17.82) * mm, "end": v(138.2, 17.82) * mm});
            skLineSegment(sketch, "E33.13.3.0", {"start": v(127.65, 19.2) * mm, "end": v(133.45, 19.2) * mm});
            skLineSegment(sketch, "E33.13.3.1", {"start": v(133.45, 19.2) * mm, "end": v(130.55, 24.22) * mm});
            skLineSegment(sketch, "E33.13.3.2", {"start": v(130.55, 24.22) * mm, "end": v(127.65, 19.2) * mm});
            skLineSegment(sketch, "E33.13.3.3", {"start": v(135.3, 19.2) * mm, "end": v(132.4, 24.22) * mm});
            skLineSegment(sketch, "E33.13.3.4", {"start": v(138.2, 24.22) * mm, "end": v(135.3, 19.2) * mm});
            skLineSegment(sketch, "E33.13.3.5", {"start": v(132.4, 24.22) * mm, "end": v(138.2, 24.22) * mm});
            skLineSegment(sketch, "E33.13.4.0", {"start": v(127.65, 25.6) * mm, "end": v(133.45, 25.6) * mm});
            skLineSegment(sketch, "E33.13.4.1", {"start": v(133.45, 25.6) * mm, "end": v(130.55, 30.62) * mm});
            skLineSegment(sketch, "E33.13.4.2", {"start": v(130.55, 30.62) * mm, "end": v(127.65, 25.6) * mm});
            skLineSegment(sketch, "E33.13.4.3", {"start": v(135.3, 25.6) * mm, "end": v(132.4, 30.62) * mm});
            skLineSegment(sketch, "E33.13.4.4", {"start": v(138.2, 30.62) * mm, "end": v(135.3, 25.6) * mm});
            skLineSegment(sketch, "E33.13.4.5", {"start": v(132.4, 30.62) * mm, "end": v(138.2, 30.62) * mm});
            skLineSegment(sketch, "E33.13.5.0", {"start": v(127.65, 32) * mm, "end": v(133.45, 32) * mm});
            skLineSegment(sketch, "E33.13.5.1", {"start": v(133.45, 32) * mm, "end": v(130.55, 37.02) * mm});
            skLineSegment(sketch, "E33.13.5.2", {"start": v(130.55, 37.02) * mm, "end": v(127.65, 32) * mm});
            skLineSegment(sketch, "E33.13.5.3", {"start": v(135.3, 32) * mm, "end": v(132.4, 37.02) * mm});
            skLineSegment(sketch, "E33.13.5.4", {"start": v(138.2, 37.02) * mm, "end": v(135.3, 32) * mm});
            skLineSegment(sketch, "E33.13.5.5", {"start": v(132.4, 37.02) * mm, "end": v(138.2, 37.02) * mm});
            skLineSegment(sketch, "E33.13.6.0", {"start": v(127.65, 38.4) * mm, "end": v(133.45, 38.4) * mm});
            skLineSegment(sketch, "E33.13.6.1", {"start": v(133.45, 38.4) * mm, "end": v(130.55, 43.42) * mm});
            skLineSegment(sketch, "E33.13.6.2", {"start": v(130.55, 43.42) * mm, "end": v(127.65, 38.4) * mm});
            skLineSegment(sketch, "E33.13.6.3", {"start": v(135.3, 38.4) * mm, "end": v(132.4, 43.42) * mm});
            skLineSegment(sketch, "E33.13.6.4", {"start": v(138.2, 43.42) * mm, "end": v(135.3, 38.4) * mm});
            skLineSegment(sketch, "E33.13.6.5", {"start": v(132.4, 43.42) * mm, "end": v(138.2, 43.42) * mm});
            skLineSegment(sketch, "E33.13.7.0", {"start": v(127.65, 44.8) * mm, "end": v(133.45, 44.8) * mm});
            skLineSegment(sketch, "E33.13.7.1", {"start": v(133.45, 44.8) * mm, "end": v(130.55, 49.82) * mm});
            skLineSegment(sketch, "E33.13.7.2", {"start": v(130.55, 49.82) * mm, "end": v(127.65, 44.8) * mm});
            skLineSegment(sketch, "E33.13.7.3", {"start": v(135.3, 44.8) * mm, "end": v(132.4, 49.82) * mm});
            skLineSegment(sketch, "E33.13.7.4", {"start": v(138.2, 49.82) * mm, "end": v(135.3, 44.8) * mm});
            skLineSegment(sketch, "E33.13.7.5", {"start": v(132.4, 49.82) * mm, "end": v(138.2, 49.82) * mm});
            skLineSegment(sketch, "E33.13.8.0", {"start": v(127.65, 51.2) * mm, "end": v(133.45, 51.2) * mm});
            skLineSegment(sketch, "E33.13.8.1", {"start": v(133.45, 51.2) * mm, "end": v(130.55, 56.22) * mm});
            skLineSegment(sketch, "E33.13.8.2", {"start": v(130.55, 56.22) * mm, "end": v(127.65, 51.2) * mm});
            skLineSegment(sketch, "E33.13.8.3", {"start": v(135.3, 51.2) * mm, "end": v(132.4, 56.22) * mm});
            skLineSegment(sketch, "E33.13.8.4", {"start": v(138.2, 56.22) * mm, "end": v(135.3, 51.2) * mm});
            skLineSegment(sketch, "E33.13.8.5", {"start": v(132.4, 56.22) * mm, "end": v(138.2, 56.22) * mm});
            skLineSegment(sketch, "E33.13.9.0", {"start": v(127.65, 57.6) * mm, "end": v(133.45, 57.6) * mm});
            skLineSegment(sketch, "E33.13.9.1", {"start": v(133.45, 57.6) * mm, "end": v(130.55, 62.62) * mm});
            skLineSegment(sketch, "E33.13.9.2", {"start": v(130.55, 62.62) * mm, "end": v(127.65, 57.6) * mm});
            skLineSegment(sketch, "E33.13.9.3", {"start": v(135.3, 57.6) * mm, "end": v(132.4, 62.62) * mm});
            skLineSegment(sketch, "E33.13.9.4", {"start": v(138.2, 62.62) * mm, "end": v(135.3, 57.6) * mm});
            skLineSegment(sketch, "E33.13.9.5", {"start": v(132.4, 62.62) * mm, "end": v(138.2, 62.62) * mm});
            skLineSegment(sketch, "E33.14.0.0", {"start": v(137.25, 0) * mm, "end": v(143.05, 0) * mm});
            skLineSegment(sketch, "E33.14.0.1", {"start": v(143.05, 0) * mm, "end": v(140.15, 5.02) * mm});
            skLineSegment(sketch, "E33.14.0.2", {"start": v(140.15, 5.02) * mm, "end": v(137.25, 0) * mm});
            skLineSegment(sketch, "E33.14.0.3", {"start": v(144.9, 0) * mm, "end": v(142, 5.02) * mm});
            skLineSegment(sketch, "E33.14.0.4", {"start": v(147.8, 5.02) * mm, "end": v(144.9, 0) * mm});
            skLineSegment(sketch, "E33.14.0.5", {"start": v(142, 5.02) * mm, "end": v(147.8, 5.02) * mm});
            skLineSegment(sketch, "E33.14.1.0", {"start": v(137.25, 6.4) * mm, "end": v(143.05, 6.4) * mm});
            skLineSegment(sketch, "E33.14.1.1", {"start": v(143.05, 6.4) * mm, "end": v(140.15, 11.42) * mm});
            skLineSegment(sketch, "E33.14.1.2", {"start": v(140.15, 11.42) * mm, "end": v(137.25, 6.4) * mm});
            skLineSegment(sketch, "E33.14.1.3", {"start": v(144.9, 6.4) * mm, "end": v(142, 11.42) * mm});
            skLineSegment(sketch, "E33.14.1.4", {"start": v(147.8, 11.42) * mm, "end": v(144.9, 6.4) * mm});
            skLineSegment(sketch, "E33.14.1.5", {"start": v(142, 11.42) * mm, "end": v(147.8, 11.42) * mm});
            skLineSegment(sketch, "E33.14.2.0", {"start": v(137.25, 12.8) * mm, "end": v(143.05, 12.8) * mm});
            skLineSegment(sketch, "E33.14.2.1", {"start": v(143.05, 12.8) * mm, "end": v(140.15, 17.82) * mm});
            skLineSegment(sketch, "E33.14.2.2", {"start": v(140.15, 17.82) * mm, "end": v(137.25, 12.8) * mm});
            skLineSegment(sketch, "E33.14.2.3", {"start": v(144.9, 12.8) * mm, "end": v(142, 17.82) * mm});
            skLineSegment(sketch, "E33.14.2.4", {"start": v(147.8, 17.82) * mm, "end": v(144.9, 12.8) * mm});
            skLineSegment(sketch, "E33.14.2.5", {"start": v(142, 17.82) * mm, "end": v(147.8, 17.82) * mm});
            skLineSegment(sketch, "E33.14.3.0", {"start": v(137.25, 19.2) * mm, "end": v(143.05, 19.2) * mm});
            skLineSegment(sketch, "E33.14.3.1", {"start": v(143.05, 19.2) * mm, "end": v(140.15, 24.22) * mm});
            skLineSegment(sketch, "E33.14.3.2", {"start": v(140.15, 24.22) * mm, "end": v(137.25, 19.2) * mm});
            skLineSegment(sketch, "E33.14.3.3", {"start": v(144.9, 19.2) * mm, "end": v(142, 24.22) * mm});
            skLineSegment(sketch, "E33.14.3.4", {"start": v(147.8, 24.22) * mm, "end": v(144.9, 19.2) * mm});
            skLineSegment(sketch, "E33.14.3.5", {"start": v(142, 24.22) * mm, "end": v(147.8, 24.22) * mm});
            skLineSegment(sketch, "E33.14.4.0", {"start": v(137.25, 25.6) * mm, "end": v(143.05, 25.6) * mm});
            skLineSegment(sketch, "E33.14.4.1", {"start": v(143.05, 25.6) * mm, "end": v(140.15, 30.62) * mm});
            skLineSegment(sketch, "E33.14.4.2", {"start": v(140.15, 30.62) * mm, "end": v(137.25, 25.6) * mm});
            skLineSegment(sketch, "E33.14.4.3", {"start": v(144.9, 25.6) * mm, "end": v(142, 30.62) * mm});
            skLineSegment(sketch, "E33.14.4.4", {"start": v(147.8, 30.62) * mm, "end": v(144.9, 25.6) * mm});
            skLineSegment(sketch, "E33.14.4.5", {"start": v(142, 30.62) * mm, "end": v(147.8, 30.62) * mm});
            skLineSegment(sketch, "E33.14.5.0", {"start": v(137.25, 32) * mm, "end": v(143.05, 32) * mm});
            skLineSegment(sketch, "E33.14.5.1", {"start": v(143.05, 32) * mm, "end": v(140.15, 37.02) * mm});
            skLineSegment(sketch, "E33.14.5.2", {"start": v(140.15, 37.02) * mm, "end": v(137.25, 32) * mm});
            skLineSegment(sketch, "E33.14.5.3", {"start": v(144.9, 32) * mm, "end": v(142, 37.02) * mm});
            skLineSegment(sketch, "E33.14.5.4", {"start": v(147.8, 37.02) * mm, "end": v(144.9, 32) * mm});
            skLineSegment(sketch, "E33.14.5.5", {"start": v(142, 37.02) * mm, "end": v(147.8, 37.02) * mm});
            skLineSegment(sketch, "E33.14.6.0", {"start": v(137.25, 38.4) * mm, "end": v(143.05, 38.4) * mm});
            skLineSegment(sketch, "E33.14.6.1", {"start": v(143.05, 38.4) * mm, "end": v(140.15, 43.42) * mm});
            skLineSegment(sketch, "E33.14.6.2", {"start": v(140.15, 43.42) * mm, "end": v(137.25, 38.4) * mm});
            skLineSegment(sketch, "E33.14.6.3", {"start": v(144.9, 38.4) * mm, "end": v(142, 43.42) * mm});
            skLineSegment(sketch, "E33.14.6.4", {"start": v(147.8, 43.42) * mm, "end": v(144.9, 38.4) * mm});
            skLineSegment(sketch, "E33.14.6.5", {"start": v(142, 43.42) * mm, "end": v(147.8, 43.42) * mm});
            skLineSegment(sketch, "E33.14.7.0", {"start": v(137.25, 44.8) * mm, "end": v(143.05, 44.8) * mm});
            skLineSegment(sketch, "E33.14.7.1", {"start": v(143.05, 44.8) * mm, "end": v(140.15, 49.82) * mm});
            skLineSegment(sketch, "E33.14.7.2", {"start": v(140.15, 49.82) * mm, "end": v(137.25, 44.8) * mm});
            skLineSegment(sketch, "E33.14.7.3", {"start": v(144.9, 44.8) * mm, "end": v(142, 49.82) * mm});
            skLineSegment(sketch, "E33.14.7.4", {"start": v(147.8, 49.82) * mm, "end": v(144.9, 44.8) * mm});
            skLineSegment(sketch, "E33.14.7.5", {"start": v(142, 49.82) * mm, "end": v(147.8, 49.82) * mm});
            skLineSegment(sketch, "E33.14.8.0", {"start": v(137.25, 51.2) * mm, "end": v(143.05, 51.2) * mm});
            skLineSegment(sketch, "E33.14.8.1", {"start": v(143.05, 51.2) * mm, "end": v(140.15, 56.22) * mm});
            skLineSegment(sketch, "E33.14.8.2", {"start": v(140.15, 56.22) * mm, "end": v(137.25, 51.2) * mm});
            skLineSegment(sketch, "E33.14.8.3", {"start": v(144.9, 51.2) * mm, "end": v(142, 56.22) * mm});
            skLineSegment(sketch, "E33.14.8.4", {"start": v(147.8, 56.22) * mm, "end": v(144.9, 51.2) * mm});
            skLineSegment(sketch, "E33.14.8.5", {"start": v(142, 56.22) * mm, "end": v(147.8, 56.22) * mm});
            skLineSegment(sketch, "E33.14.9.0", {"start": v(137.25, 57.6) * mm, "end": v(143.05, 57.6) * mm});
            skLineSegment(sketch, "E33.14.9.1", {"start": v(143.05, 57.6) * mm, "end": v(140.15, 62.62) * mm});
            skLineSegment(sketch, "E33.14.9.2", {"start": v(140.15, 62.62) * mm, "end": v(137.25, 57.6) * mm});
            skLineSegment(sketch, "E33.14.9.3", {"start": v(144.9, 57.6) * mm, "end": v(142, 62.62) * mm});
            skLineSegment(sketch, "E33.14.9.4", {"start": v(147.8, 62.62) * mm, "end": v(144.9, 57.6) * mm});
            skLineSegment(sketch, "E33.14.9.5", {"start": v(142, 62.62) * mm, "end": v(147.8, 62.62) * mm});
            skLineSegment(sketch, "E33.direction1", {"start": v(2.85, 0) * mm, "end": v(12.45, 0) * mm, "construction": true});
            skLineSegment(sketch, "E33.direction2", {"start": v(2.85, 0) * mm, "end": v(2.85, 6.4) * mm, "construction": true});
            skSolve(sketch);
        }
        {
            var Q0;
            Q0=makeQuery(id+"F3.imprint","IMPRINT",FACE,{"disambiguationData":[TD([[makeQuery(id+"F3.imprint","IMPRINT",EDGE,{"derivedFrom":sQuery(id+"F3.wireOp",EDGE,"E27")}),-1.0]])]});
            extrude(context, id + "F4", {"entities" : qUnion([Q0]), "operationType" : NewBodyOperationType.INTERSECT, "oppositeDirection" : true, "depth" : 25 * mm});
        }
        {
            var Q0;
            Q0=makeQuery(id+"F0.imprint","IMPRINT",FACE,{"disambiguationData":[TD([[makeQuery(id+"F0.imprint","IMPRINT",EDGE,{"derivedFrom":sQuery(id+"F0.wireOp",EDGE,"E0")}),-1.0]])]});
            extrude(context, id + "F5", {"entities" : qUnion([Q0]), "depth" : 150 * mm});
        }
        {
            var Q0;
            Q0=makeQuery(id+"F5.opExtrude","SWEPT_BODY",BODY,{"disambiguationData":[OSD([sQuery(id+"F0.wireOp",EDGE,"E0"),sQuery(id+"F0.wireOp",EDGE,"E2"),sQuery(id+"F0.wireOp",EDGE,"E4"),sQuery(id+"F0.wireOp",EDGE,"E5"),sQuery(id+"F0.wireOp",EDGE,"E6"),sQuery(id+"F0.wireOp",EDGE,"E7"),sQuery(id+"F0.wireOp",EDGE,"E8")])]});
            var Q1;
            Q1=makeQuery(id+"F1.opExtrude","SWEPT_BODY",BODY,{"disambiguationData":[OSD([sQuery(id+"F0.wireOp",EDGE,"E0"),sQuery(id+"F0.wireOp",EDGE,"E1"),sQuery(id+"F0.wireOp",EDGE,"E2"),sQuery(id+"F0.wireOp",EDGE,"E3"),sQuery(id+"F0.wireOp",EDGE,"E4"),sQuery(id+"F0.wireOp",EDGE,"E5"),sQuery(id+"F0.wireOp",EDGE,"E6"),sQuery(id+"F0.wireOp",EDGE,"E7")])]});
            booleanBodies(context, id + "F6", {"operationType" : BooleanOperationType.UNION, "tools" : qUnion([Q0, Q1])});
        }
        {
            var Q0;
            Q0=makeQuery(id+"F2.imprint","IMPRINT",FACE,{"disambiguationData":[TD([[makeQuery(id+"F2.imprint","IMPRINT",EDGE,{"derivedFrom":sQuery(id+"F2.wireOp",EDGE,"E17.MirrorC")}),1.0]])]});
            var Q1;
            Q1=makeQuery(id+"F2.imprint","IMPRINT",FACE,{"disambiguationData":[TD([[makeQuery(id+"F2.imprint","IMPRINT",EDGE,{"derivedFrom":sQuery(id+"F2.wireOp",EDGE,"bfd0f448-6e91-4b74-8a5b-a1f346314e810.MirrorC")}),-1.0]])]});
            extrude(context, id + "F7", {"entities" : qUnion([Q0, Q1]), "operationType" : NewBodyOperationType.REMOVE, "oppositeDirection" : true, "depth" : 25 * mm});
        }
        {
            var Q0;
            Q0=makeQuery(id+"F2.imprint","IMPRINT",FACE,{"disambiguationData":[TD([[makeQuery(id+"F2.imprint","IMPRINT",EDGE,{"derivedFrom":sQuery(id+"F2.wireOp",EDGE,"bfd0f448-6e91-4b74-8a5b-a1f346314e810.MirrorC")}),1.0]])]});
            var Q1;
            Q1=makeQuery(id+"F2.imprint","IMPRINT",FACE,{"disambiguationData":[TD([[makeQuery(id+"F2.imprint","IMPRINT",EDGE,{"derivedFrom":sQuery(id+"F2.wireOp",EDGE,"80617300-e3b3-4370-a104-ddc893ad95890.MirrorC")}),-1.0]])]});
            var Q2;
            Q2=makeQuery(id+"F2.imprint","IMPRINT",FACE,{"disambiguationData":[TD([[makeQuery(id+"F2.imprint","IMPRINT",EDGE,{"derivedFrom":sQuery(id+"F2.wireOp",EDGE,"E20.MirrorC")}),1.0]])]});
            var Q3;
            Q3=makeQuery(id+"F2.imprint","IMPRINT",FACE,{"disambiguationData":[TD([[makeQuery(id+"F2.imprint","IMPRINT",EDGE,{"derivedFrom":sQuery(id+"F2.wireOp",EDGE,"E17.MirrorC")}),-1.0]])]});
            var Q4;
            Q4=makeQuery(id+"F2.imprint","IMPRINT",FACE,{"disambiguationData":[TD([[makeQuery(id+"F2.imprint","IMPRINT",EDGE,{"derivedFrom":sQuery(id+"F2.wireOp",EDGE,"E23.MirrorC")}),1.0]])]});
            var Q5;
            Q5=makeQuery(id+"F2.imprint","IMPRINT",FACE,{"disambiguationData":[TD([[makeQuery(id+"F2.imprint","IMPRINT",EDGE,{"derivedFrom":sQuery(id+"F2.wireOp",EDGE,"E25.MirrorC")}),-1.0]])]});
            var Q6;
            Q6=sQuery(id+"F2.wireOp",EDGE,"gWZW0fD7-YT0C-o7pO-Ghny-xo6oIcKr0HY7");
            var Q7;
            Q7=sQuery(id+"F2.wireOp",EDGE,"E18.MirrorC");
            var Q8;
            Q8=makeQuery(id+"F1.opExtrude","SWEPT_FACE",FACE,{"disambiguationData":[OSD([sQuery(id+"F0.wireOp",EDGE,"E1")])]});
            extrude(context, id + "F8", {"entities" : qUnion([Q0, Q1, Q2, Q3, Q4, Q5]), "operationType" : NewBodyOperationType.ADD, "surfaceEntities" : qUnion([Q6, Q7]), "endBound" : BoundingType.UP_TO_SURFACE, "oppositeDirection" : true, "endBoundEntityFace" : qUnion([Q8]), "depth" : 25 * mm});
        }
        {
            var Q0;
            Q0=makeQuery(id+"F2.imprint","IMPRINT",FACE,{"disambiguationData":[TD([[makeQuery(id+"F2.imprint","IMPRINT",EDGE,{"derivedFrom":sQuery(id+"F2.wireOp",EDGE,"80617300-e3b3-4370-a104-ddc893ad95890.MirrorC")}),1.0]])]});
            var Q1;
            Q1=makeQuery(id+"F2.imprint","IMPRINT",FACE,{"disambiguationData":[TD([[makeQuery(id+"F2.imprint","IMPRINT",EDGE,{"derivedFrom":sQuery(id+"F2.wireOp",EDGE,"E21.MirrorC")}),-1.0]])]});
            var Q2;
            Q2=makeQuery(id+"F2.imprint","IMPRINT",FACE,{"disambiguationData":[TD([[makeQuery(id+"F2.imprint","IMPRINT",EDGE,{"derivedFrom":sQuery(id+"F2.wireOp",EDGE,"E23.MirrorC")}),-1.0]])]});
            var Q3;
            Q3=makeQuery(id+"F2.imprint","IMPRINT",FACE,{"disambiguationData":[TD([[makeQuery(id+"F2.imprint","IMPRINT",EDGE,{"derivedFrom":sQuery(id+"F2.wireOp",EDGE,"E25.MirrorC")}),1.0]])]});
            var Q4;
            Q4=makeQuery(id+"F8.boolean.opBoolean","MERGE",FACE,{"derivedFrom":[makeQuery(id+"F1.opExtrude","SWEPT_FACE",FACE,{"disambiguationData":[OSD([sQuery(id+"F0.wireOp",EDGE,"E1")])]}),makeQuery(id+"F8.opExtrude","CAP_FACE",FACE,{"disambiguationData":[OSD([sQuery(id+"F2.wireOp",EDGE,"E17.MirrorC"),sQuery(id+"F2.wireOp",EDGE,"E18.MirrorC")])],"isStart":false}),makeQuery(id+"F8.opExtrude","CAP_FACE",FACE,{"disambiguationData":[OSD([sQuery(id+"F2.wireOp",EDGE,"E20.MirrorC"),sQuery(id+"F2.wireOp",EDGE,"E21.MirrorC")])],"isStart":false}),makeQuery(id+"F8.opExtrude","CAP_FACE",FACE,{"disambiguationData":[OSD([sQuery(id+"F2.wireOp",EDGE,"E23.MirrorC"),sQuery(id+"F2.wireOp",EDGE,"E24.MirrorC")])],"isStart":false}),makeQuery(id+"F8.opExtrude","CAP_FACE",FACE,{"disambiguationData":[OSD([sQuery(id+"F2.wireOp",EDGE,"E25.MirrorC"),sQuery(id+"F2.wireOp",EDGE,"E26.MirrorC")])],"isStart":false})]});
            extrude(context, id + "F9", {"entities" : qUnion([Q0, Q1, Q2, Q3]), "operationType" : NewBodyOperationType.REMOVE, "endBound" : BoundingType.UP_TO_SURFACE, "oppositeDirection" : true, "endBoundEntityFace" : qUnion([Q4]), "depth" : 25 * mm});
        }
        {
            var Q0;
            Q0=makeQuery(id+"F0.imprint","IMPRINT",FACE,{"disambiguationData":[TD([[makeQuery(id+"F0.imprint","IMPRINT",EDGE,{"derivedFrom":sQuery(id+"F0.wireOp",EDGE,"E11.MirrorCS")}),1.0]])]});
            var Q1;
            {var subQ0=sQuery(id+"F0.wireOp",EDGE,"E10");var subQ1=sQuery(id+"F0.wireOp",EDGE,"E7");var subQ2=sQuery(id+"F0.wireOp",EDGE,"E6");var subQ3=sQuery(id+"F0.wireOp",EDGE,"E5");var subQ4=sQuery(id+"F0.wireOp",EDGE,"E2");var subQ5=sQuery(id+"F0.wireOp",EDGE,"E0");Q1=makeQuery(id+"F6.opBoolean","MERGE",FACE,{"derivedFrom":[makeQuery(id+"F1.opExtrude","CAP_FACE",FACE,{"disambiguationData":[OSD([subQ5,sQuery(id+"F0.wireOp",EDGE,"E1"),subQ4,sQuery(id+"F0.wireOp",EDGE,"E4"),subQ3,subQ2,subQ1,subQ0,sQuery(id+"F0.wireOp",EDGE,"E11.MirrorCS"),sQuery(id+"F0.wireOp",EDGE,"E12.MirrorCS"),sQuery(id+"F0.wireOp",EDGE,"E13.MirrorCS"),sQuery(id+"F0.wireOp",EDGE,"E14.MirrorCS"),sQuery(id+"F0.wireOp",EDGE,"E15.MirrorCS"),sQuery(id+"F0.wireOp",EDGE,"E16.MirrorCS")])],"isStart":false}),makeQuery(id+"F5.opExtrude","CAP_FACE",FACE,{"disambiguationData":[OSD([subQ5,subQ4,subQ3,subQ2,subQ1,sQuery(id+"F0.wireOp",EDGE,"E8"),subQ0])],"isStart":false})]});}
            extrude(context, id + "F10", {"entities" : qUnion([Q0]), "operationType" : NewBodyOperationType.ADD, "endBound" : BoundingType.UP_TO_SURFACE, "endBoundEntityFace" : qUnion([Q1]), "depth" : 25 * mm});
        }
        {
            var Q0;
            Q0=makeQuery(id+"F5.opExtrude","SWEPT_EDGE",EDGE,{"disambiguationData":[OSD([sQuery(id+"F0.wireOp",EDGE,"E0"),sQuery(id+"F0.wireOp",EDGE,"E2")])]});
            var Q1;
            Q1=makeQuery(id+"F10.opExtrude","SWEPT_EDGE",EDGE,{"disambiguationData":[OSD([sQuery(id+"F0.wireOp",EDGE,"E13.MirrorCS"),sQuery(id+"F0.wireOp",EDGE,"E14.MirrorCS")])]});
            chamfer(context, id + "F11", {"entities" : qUnion([Q0, Q1]), "chamferType" : ChamferType.OFFSET_ANGLE, "width" : 2.4 * mm, "oppositeDirection" : false, "angle" : 53 * degree, "tangentPropagation" : true});
        }
        {
            var Q0;
            Q0=makeQuery(id+"F5.opExtrude","SWEPT_EDGE",EDGE,{"disambiguationData":[OSD([sQuery(id+"F0.wireOp",EDGE,"E5"),sQuery(id+"F0.wireOp",EDGE,"E6")])]});
            var Q1;
            Q1=makeQuery(id+"F5.opExtrude","SWEPT_EDGE",EDGE,{"disambiguationData":[OSD([sQuery(id+"F0.wireOp",EDGE,"E6"),sQuery(id+"F0.wireOp",EDGE,"E7")])]});
            var Q2;
            Q2=makeQuery(id+"F10.opExtrude","SWEPT_EDGE",EDGE,{"disambiguationData":[OSD([sQuery(id+"F0.wireOp",EDGE,"E11.MirrorCS"),sQuery(id+"F0.wireOp",EDGE,"E12.MirrorCS")])]});
            var Q3;
            Q3=makeQuery(id+"F10.opExtrude","SWEPT_EDGE",EDGE,{"disambiguationData":[OSD([sQuery(id+"F0.wireOp",EDGE,"E11.MirrorCS"),sQuery(id+"F0.wireOp",EDGE,"E16.MirrorCS")])]});
            var Q4;
            Q4=makeQuery(id+"F5.opExtrude","SWEPT_EDGE",EDGE,{"disambiguationData":[OSD([sQuery(id+"F0.wireOp",EDGE,"E5"),sQuery(id+"F0.wireOp",EDGE,"E10")])]});
            var Q5;
            Q5=makeQuery(id+"F10.opExtrude","SWEPT_EDGE",EDGE,{"disambiguationData":[OSD([sQuery(id+"F0.wireOp",EDGE,"E15.MirrorCS"),sQuery(id+"F0.wireOp",EDGE,"E16.MirrorCS")])]});
            var Q6;
            Q6=makeQuery(id+"F1.opExtrude","CAP_EDGE",EDGE,{"disambiguationData":[OSD([sQuery(id+"F0.wireOp",EDGE,"E1")])],"isStart":true});
            var Q7;
            {var subQ0=sQuery(id+"F0.wireOp",EDGE,"E15.MirrorCS");var subQ1=sQuery(id+"F0.wireOp",EDGE,"E10");Q7=makeQuery(id+"F10.boolean.opBoolean","MERGE",EDGE,{"derivedFrom":[makeQuery(id+"F6.opBoolean","MERGE",EDGE,{"derivedFrom":[makeQuery(id+"F1.opExtrude","CAP_EDGE",EDGE,{"disambiguationData":[OSD([sQuery(id+"F0.wireOp",EDGE,"E4"),subQ1,subQ0])],"isStart":true}),makeQuery(id+"F5.opExtrude","CAP_EDGE",EDGE,{"disambiguationData":[OSD([subQ1])],"isStart":true})]}),makeQuery(id+"F10.opExtrude","CAP_EDGE",EDGE,{"disambiguationData":[OSD([subQ0])],"isStart":true})]});}
            var Q8;
            Q8=makeQuery(id+"F10.opExtrude","CAP_EDGE",EDGE,{"disambiguationData":[OSD([sQuery(id+"F0.wireOp",EDGE,"E3"),sQuery(id+"F0.wireOp",EDGE,"E14.MirrorCS")])],"isStart":true});
            var Q9;
            Q9=makeQuery(id+"F10.opExtrude","CAP_EDGE",EDGE,{"disambiguationData":[OSD([sQuery(id+"F0.wireOp",EDGE,"E16.MirrorCS")])],"isStart":true});
            var Q10;
            Q10=makeQuery(id+"F5.opExtrude","CAP_EDGE",EDGE,{"disambiguationData":[OSD([sQuery(id+"F0.wireOp",EDGE,"E5")])],"isStart":true});
            var Q11;
            Q11=makeQuery(id+"F5.opExtrude","CAP_EDGE",EDGE,{"disambiguationData":[OSD([sQuery(id+"F0.wireOp",EDGE,"E0"),sQuery(id+"F0.wireOp",EDGE,"E8")])],"isStart":true});
            var Q12;
            Q12=makeQuery(id+"F1.opExtrude","CAP_EDGE",EDGE,{"disambiguationData":[OSD([sQuery(id+"F0.wireOp",EDGE,"E1")])],"isStart":false});
            var Q13;
            Q13=makeQuery(id+"F5.opExtrude","CAP_EDGE",EDGE,{"disambiguationData":[OSD([sQuery(id+"F0.wireOp",EDGE,"E5")])],"isStart":false});
            var Q14;
            Q14=makeQuery(id+"F5.opExtrude","CAP_EDGE",EDGE,{"disambiguationData":[OSD([sQuery(id+"F0.wireOp",EDGE,"E0"),sQuery(id+"F0.wireOp",EDGE,"E8")])],"isStart":false});
            var Q15;
            Q15=makeQuery(id+"F10.opExtrude","CAP_EDGE",EDGE,{"disambiguationData":[OSD([sQuery(id+"F0.wireOp",EDGE,"E3"),sQuery(id+"F0.wireOp",EDGE,"E14.MirrorCS")])],"isStart":false});
            var Q16;
            Q16=makeQuery(id+"F10.opExtrude","CAP_EDGE",EDGE,{"disambiguationData":[OSD([sQuery(id+"F0.wireOp",EDGE,"E16.MirrorCS")])],"isStart":false});
            var Q17;
            {var subQ0=sQuery(id+"F0.wireOp",EDGE,"E15.MirrorCS");var subQ1=sQuery(id+"F0.wireOp",EDGE,"E10");Q17=makeQuery(id+"F10.boolean.opBoolean","MERGE",EDGE,{"derivedFrom":[makeQuery(id+"F6.opBoolean","MERGE",EDGE,{"derivedFrom":[makeQuery(id+"F1.opExtrude","CAP_EDGE",EDGE,{"disambiguationData":[OSD([sQuery(id+"F0.wireOp",EDGE,"E4"),subQ1,subQ0])],"isStart":false}),makeQuery(id+"F5.opExtrude","CAP_EDGE",EDGE,{"disambiguationData":[OSD([subQ1])],"isStart":false})]}),makeQuery(id+"F10.opExtrude","CAP_EDGE",EDGE,{"disambiguationData":[OSD([subQ0])],"isStart":false})]});}
            var Q18;
            {var subQ0=sQuery(id+"F0.wireOp",EDGE,"E14.MirrorCS");var subQ1=sQuery(id+"F0.wireOp",EDGE,"E3");var subQ2=sQuery(id+"F0.wireOp",EDGE,"E1");Q18=makeQuery(id+"F4.boolean.opBoolean","MERGE",EDGE,{"derivedFrom":[makeQuery(id+"F1.opExtrude","SWEPT_EDGE",EDGE,{"disambiguationData":[OSD([subQ2,subQ1,subQ0])]}),makeQuery(id+"F4.boolean.toolComplement.opBoolean","COPY",EDGE,{"derivedFrom":makeQuery(id+"F4.opExtrude","CAP_EDGE",EDGE,{"disambiguationData":[OSD([subQ2,subQ1,subQ0])],"isStart":true})})]});}
            var Q19;
            {var subQ0=sQuery(id+"F0.wireOp",EDGE,"E8");var subQ1=sQuery(id+"F0.wireOp",EDGE,"E1");var subQ2=sQuery(id+"F0.wireOp",EDGE,"E0");Q19=makeQuery(id+"F4.boolean.opBoolean","MERGE",EDGE,{"derivedFrom":[makeQuery(id+"F1.opExtrude","SWEPT_EDGE",EDGE,{"disambiguationData":[OSD([subQ2,subQ1,subQ0])]}),makeQuery(id+"F4.boolean.toolComplement.opBoolean","COPY",EDGE,{"derivedFrom":makeQuery(id+"F4.opExtrude","CAP_EDGE",EDGE,{"disambiguationData":[OSD([subQ2,subQ1,subQ0])],"isStart":true})})]});}
            var Q20;
            Q20=makeQuery(id+"F10.opExtrude","CAP_EDGE",EDGE,{"disambiguationData":[OSD([sQuery(id+"F0.wireOp",EDGE,"E11.MirrorCS")])],"isStart":false});
            var Q21;
            Q21=makeQuery(id+"F5.opExtrude","CAP_EDGE",EDGE,{"disambiguationData":[OSD([sQuery(id+"F0.wireOp",EDGE,"E6")])],"isStart":false});
            var Q22;
            Q22=makeQuery(id+"F10.opExtrude","CAP_EDGE",EDGE,{"disambiguationData":[OSD([sQuery(id+"F0.wireOp",EDGE,"E11.MirrorCS")])],"isStart":true});
            var Q23;
            Q23=makeQuery(id+"F5.opExtrude","CAP_EDGE",EDGE,{"disambiguationData":[OSD([sQuery(id+"F0.wireOp",EDGE,"E6")])],"isStart":true});
            var Q24;
            Q24=makeQuery(id+"F5.opExtrude","CAP_EDGE",EDGE,{"disambiguationData":[OSD([sQuery(id+"F0.wireOp",EDGE,"E7")])],"isStart":false});
            var Q25;
            Q25=makeQuery(id+"F10.opExtrude","CAP_EDGE",EDGE,{"disambiguationData":[OSD([sQuery(id+"F0.wireOp",EDGE,"E12.MirrorCS")])],"isStart":false});
            var Q26;
            Q26=makeQuery(id+"F5.opExtrude","CAP_EDGE",EDGE,{"disambiguationData":[OSD([sQuery(id+"F0.wireOp",EDGE,"E7")])],"isStart":true});
            var Q27;
            Q27=makeQuery(id+"F10.opExtrude","CAP_EDGE",EDGE,{"disambiguationData":[OSD([sQuery(id+"F0.wireOp",EDGE,"E12.MirrorCS")])],"isStart":true});
            fillet(context, id + "F12", {"entities" : qUnion([Q0, Q1, Q2, Q3, Q4, Q5, Q6, Q7, Q8, Q9, Q10, Q11, Q12, Q13, Q14, Q15, Q16, Q17, Q18, Q19, Q20, Q21, Q22, Q23, Q24, Q25, Q26, Q27]), "radius" : 1 * mm, "tangentPropagation" : true, "allowEdgeOverflow" : false});
        }
        {
            var Q0;
            Q0=makeQuery(id+"F8.boolean.opBoolean","MERGE",FACE,{"derivedFrom":[makeQuery(id+"F1.opExtrude","SWEPT_FACE",FACE,{"disambiguationData":[OSD([sQuery(id+"F0.wireOp",EDGE,"E1")])]}),makeQuery(id+"F8.opExtrude","CAP_FACE",FACE,{"disambiguationData":[OSD([sQuery(id+"F2.wireOp",EDGE,"E17.MirrorC"),sQuery(id+"F2.wireOp",EDGE,"E18.MirrorC")])],"isStart":false}),makeQuery(id+"F8.opExtrude","CAP_FACE",FACE,{"disambiguationData":[OSD([sQuery(id+"F2.wireOp",EDGE,"E20.MirrorC"),sQuery(id+"F2.wireOp",EDGE,"E21.MirrorC")])],"isStart":false}),makeQuery(id+"F8.opExtrude","CAP_FACE",FACE,{"disambiguationData":[OSD([sQuery(id+"F2.wireOp",EDGE,"E23.MirrorC"),sQuery(id+"F2.wireOp",EDGE,"E24.MirrorC")])],"isStart":false}),makeQuery(id+"F8.opExtrude","CAP_FACE",FACE,{"disambiguationData":[OSD([sQuery(id+"F2.wireOp",EDGE,"E25.MirrorC"),sQuery(id+"F2.wireOp",EDGE,"E26.MirrorC")])],"isStart":false})]});
            var sketch = newSketch(context, id + "F13", { "sketchPlane" : qUnion([Q0])});
            skCircle(sketch, "E34.0", {"center": v(15.4, 58) * mm, "radius": 8 * mm});
            skCircle(sketch, "E34.1", {"center": v(15.4, 7.6) * mm, "radius": 8 * mm});
            skCircle(sketch, "E34.2", {"center": v(134.6, 58) * mm, "radius": 8 * mm});
            skCircle(sketch, "E34.3", {"center": v(134.6, 7.6) * mm, "radius": 8 * mm});
            skSolve(sketch);
        }
        {
            var Q0;
            {var subQ0=sQuery(id+"F13.wireOp",EDGE,"E34.0");var subQ10=makeQuery(id+"F13.imprint","INTERSECT",VERTEX,{"derivedFrom":[makeQuery(id+"F4.boolean.opBoolean","COPY",EDGE,{"derivedFrom":makeQuery(id+"F4.boolean.toolComplement.opBoolean","COPY",EDGE,{"derivedFrom":makeQuery(id+"F4.opExtrude","CAP_EDGE",EDGE,{"disambiguationData":[OSD([sQuery(id+"F3.wireOp",EDGE,"E33.1.8.3")])],"isStart":true})})}),subQ0]});Q0=makeQuery(id+"F13.imprint","IMPRINT",FACE,{"disambiguationData":[TD([[makeQuery(id+"F13.imprint","IMPRINT",EDGE,{"disambiguationData":[TD([[subQ10,1.0]])],"derivedFrom":subQ0}),-1.0]])]});}
            var Q1;
            {var subQ0=sQuery(id+"F13.wireOp",EDGE,"E34.1");var subQ30=sQuery(id+"F3.wireOp",EDGE,"E33.1.0.1");var subQ31=makeQuery(id+"F13.imprint","INTERSECT",VERTEX,{"derivedFrom":[makeQuery(id+"F4.boolean.opBoolean","COPY",EDGE,{"derivedFrom":makeQuery(id+"F4.boolean.toolComplement.opBoolean","COPY",EDGE,{"derivedFrom":makeQuery(id+"F4.opExtrude","CAP_EDGE",EDGE,{"disambiguationData":[OSD([subQ30])],"isStart":true})})}),subQ0]});Q1=makeQuery(id+"F13.imprint","IMPRINT",FACE,{"disambiguationData":[TD([[makeQuery(id+"F13.imprint","IMPRINT",EDGE,{"disambiguationData":[TD([[subQ31,-1.0]])],"derivedFrom":subQ0}),1.0]])]});}
            var Q2;
            {var subQ0=sQuery(id+"F13.wireOp",EDGE,"E34.2");var subQ8=makeQuery(id+"F13.imprint","INTERSECT",VERTEX,{"derivedFrom":[makeQuery(id+"F4.boolean.opBoolean","COPY",EDGE,{"derivedFrom":makeQuery(id+"F4.boolean.toolComplement.opBoolean","COPY",EDGE,{"derivedFrom":makeQuery(id+"F4.opExtrude","CAP_EDGE",EDGE,{"disambiguationData":[OSD([sQuery(id+"F3.wireOp",EDGE,"E33.14.8.0")])],"isStart":true})})}),subQ0]});Q2=makeQuery(id+"F13.imprint","IMPRINT",FACE,{"disambiguationData":[TD([[makeQuery(id+"F13.imprint","IMPRINT",EDGE,{"disambiguationData":[TD([[subQ8,-1.0]])],"derivedFrom":subQ0}),1.0]])]});}
            var Q3;
            {var subQ0=sQuery(id+"F13.wireOp",EDGE,"E34.3");var subQ21=makeQuery(id+"F13.imprint","INTERSECT",VERTEX,{"derivedFrom":[makeQuery(id+"F4.boolean.opBoolean","COPY",EDGE,{"derivedFrom":makeQuery(id+"F4.boolean.toolComplement.opBoolean","COPY",EDGE,{"derivedFrom":makeQuery(id+"F4.opExtrude","CAP_EDGE",EDGE,{"disambiguationData":[OSD([sQuery(id+"F3.wireOp",EDGE,"E33.12.0.4")])],"isStart":true})})}),subQ0]});Q3=makeQuery(id+"F13.imprint","IMPRINT",FACE,{"disambiguationData":[TD([[makeQuery(id+"F13.imprint","IMPRINT",EDGE,{"disambiguationData":[TD([[subQ21,1.0]])],"derivedFrom":subQ0}),-1.0]])]});}
            extrude(context, id + "F14", {"entities" : qUnion([Q0, Q1, Q2, Q3]), "operationType" : NewBodyOperationType.REMOVE, "oppositeDirection" : true, "depth" : 1.6 * mm, "offsetDistance" : 25 * mm});
        }
        {
            var Q0;
            Q0=makeQuery(id+"F10.opExtrude","SWEPT_FACE",FACE,{"disambiguationData":[OSD([sQuery(id+"F0.wireOp",EDGE,"E16.MirrorCS")])]});
            var sketch = newSketch(context, id + "F15", { "sketchPlane" : qUnion([Q0])});
            skLineSegment(sketch, "E35", {"start": v(149, -7.09) * mm, "end": v(84, -7.09) * mm, "construction": true});
            skLineSegment(sketch, "E36", {"start": v(149, -7.09) * mm, "end": v(125, -7.09) * mm, "construction": true});
            skLineSegment(sketch, "E37.bottom", {"start": v(120, -1.02) * mm, "end": v(89, -1.02) * mm});
            skLineSegment(sketch, "E37.top", {"start": v(120, -13.16) * mm, "end": v(89, -13.16) * mm});
            skLineSegment(sketch, "E37.left", {"start": v(125, -6.02) * mm, "end": v(125, -8.16) * mm});
            skLineSegment(sketch, "E37.right", {"start": v(84, -6.02) * mm, "end": v(84, -8.16) * mm});
            skPoint(sketch, "E37.middle", {"position": v(104.5, -7.09) * mm});
            skPoint(sketch, "E38.visualSharp", {"position": v(84, -1.02) * mm});
            skArc(sketch, "E38.filletArc", {"start": v(89, -1.02) * mm, "mid": v(85.46, -2.48) * mm, "end": v(84, -6.02) * mm});
            skPoint(sketch, "E39.visualSharp", {"position": v(84, -13.16) * mm});
            skArc(sketch, "E39.filletArc", {"start": v(84, -8.16) * mm, "mid": v(85.46, -11.7) * mm, "end": v(89, -13.16) * mm});
            skPoint(sketch, "E40.visualSharp", {"position": v(125, -13.16) * mm});
            skArc(sketch, "E40.filletArc", {"start": v(120, -13.16) * mm, "mid": v(123.54, -11.7) * mm, "end": v(125, -8.16) * mm});
            skPoint(sketch, "E41.visualSharp", {"position": v(125, -1.02) * mm});
            skArc(sketch, "E41.filletArc", {"start": v(125, -6.02) * mm, "mid": v(123.54, -2.48) * mm, "end": v(120, -1.02) * mm});
            skSolve(sketch);
        }
        {
            var Q0;
            Q0=makeQuery(id+"F15.imprint","IMPRINT",FACE,{"disambiguationData":[TD([[makeQuery(id+"F15.imprint","IMPRINT",EDGE,{"derivedFrom":sQuery(id+"F15.wireOp",EDGE,"E37.bottom")}),1.0]])]});
            var Q1;
            Q1=makeQuery(id+"F10.opExtrude","SWEPT_FACE",FACE,{"disambiguationData":[OSD([sQuery(id+"F0.wireOp",EDGE,"E12.MirrorCS")])]});
            extrude(context, id + "F16", {"entities" : qUnion([Q0]), "operationType" : NewBodyOperationType.REMOVE, "endBound" : BoundingType.UP_TO_SURFACE, "oppositeDirection" : true, "depth" : 25 * mm, "endBoundEntityFace" : qUnion([Q1]), "offsetDistance" : 25 * mm});
        }
        {
            var Q0;
            Q0=makeQuery(id+"F5.opExtrude","SWEPT_FACE",FACE,{"disambiguationData":[OSD([sQuery(id+"F0.wireOp",EDGE,"E5")])]});
            var sketch = newSketch(context, id + "F17", { "sketchPlane" : qUnion([Q0])});
            skLineSegment(sketch, "E42.0", {"start": v(120, 13.16) * mm, "end": v(89, 13.16) * mm});
            skArc(sketch, "E42.1", {"start": v(84, 8.16) * mm, "mid": v(85.46, 11.7) * mm, "end": v(89, 13.16) * mm});
            skLineSegment(sketch, "E42.2", {"start": v(84, 6.02) * mm, "end": v(84, 8.16) * mm});
            skArc(sketch, "E42.3", {"start": v(89, 1.02) * mm, "mid": v(85.46, 2.48) * mm, "end": v(84, 6.02) * mm});
            skLineSegment(sketch, "E42.4", {"start": v(120, 1.02) * mm, "end": v(89, 1.02) * mm});
            skArc(sketch, "E42.5", {"start": v(120, 13.16) * mm, "mid": v(123.54, 11.7) * mm, "end": v(125, 8.16) * mm});
            skArc(sketch, "E42.6", {"start": v(125, 6.02) * mm, "mid": v(123.54, 2.48) * mm, "end": v(120, 1.02) * mm});
            skLineSegment(sketch, "E42.7", {"start": v(125, 6.02) * mm, "end": v(125, 8.16) * mm});
            skLineSegment(sketch, "E43", {"start": v(1, 7.09) * mm, "end": v(149, 7.09) * mm, "construction": true});
            skLineSegment(sketch, "E44", {"start": v(75, 7.09) * mm, "end": v(75, -1.22) * mm, "construction": true});
            skArc(sketch, "E45.MirrorCS", {"start": v(61, 1.02) * mm, "mid": v(64.54, 2.48) * mm, "end": v(66, 6.02) * mm});
            skLineSegment(sketch, "E46.MirrorCS", {"start": v(66, 6.02) * mm, "end": v(66, 8.16) * mm});
            skArc(sketch, "E47.MirrorCS", {"start": v(66, 8.16) * mm, "mid": v(64.54, 11.7) * mm, "end": v(61, 13.16) * mm});
            skLineSegment(sketch, "E48.MirrorCS", {"start": v(30, 13.16) * mm, "end": v(61, 13.16) * mm});
            skArc(sketch, "E49.MirrorCS", {"start": v(30, 13.16) * mm, "mid": v(26.46, 11.7) * mm, "end": v(25, 8.16) * mm});
            skLineSegment(sketch, "E50.MirrorCS", {"start": v(30, 1.02) * mm, "end": v(61, 1.02) * mm});
            skLineSegment(sketch, "E51.MirrorCS", {"start": v(25, 6.02) * mm, "end": v(25, 8.16) * mm});
            skArc(sketch, "E52.MirrorCS", {"start": v(25, 6.02) * mm, "mid": v(26.46, 2.48) * mm, "end": v(30, 1.02) * mm});
            skSolve(sketch);
        }
        {
            var Q0;
            Q0=makeQuery(id+"F17.imprint","IMPRINT",FACE,{"disambiguationData":[TD([[makeQuery(id+"F17.imprint","IMPRINT",EDGE,{"derivedFrom":sQuery(id+"F17.wireOp",EDGE,"E45.MirrorCS")}),1.0]])]});
            var Q1;
            Q1=makeQuery(id+"F5.opExtrude","SWEPT_FACE",FACE,{"disambiguationData":[OSD([sQuery(id+"F0.wireOp",EDGE,"E0"),sQuery(id+"F0.wireOp",EDGE,"E8")])]});
            extrude(context, id + "F18", {"entities" : qUnion([Q0]), "operationType" : NewBodyOperationType.REMOVE, "endBound" : BoundingType.UP_TO_SURFACE, "oppositeDirection" : true, "depth" : 25 * mm, "endBoundEntityFace" : qUnion([Q1]), "offsetDistance" : 25 * mm});
        }
        {
            var Q0;
            Q0=makeQuery(id+"F5.opExtrude","SWEPT_FACE",FACE,{"disambiguationData":[OSD([sQuery(id+"F0.wireOp",EDGE,"E5")])]});
            var sketch = newSketch(context, id + "F19", { "sketchPlane" : qUnion([Q0])});
            skLineSegment(sketch, "E53.0", {"start": v(0, -2.22) * mm, "end": v(0, 6.4) * mm});
            skLineSegment(sketch, "E53.1", {"start": v(10, 16.4) * mm, "end": v(140, 16.4) * mm});
            skLineSegment(sketch, "E53.2", {"start": v(150, 15.4) * mm, "end": v(150, -1.22) * mm});
            skLineSegment(sketch, "E54", {"start": v(150, -1.22) * mm, "end": v(150, 6.4) * mm});
            skLineSegment(sketch, "E55", {"start": v(150, 16.4) * mm, "end": v(149, 16.4) * mm});
            skLineSegment(sketch, "E56", {"start": v(1, 16.4) * mm, "end": v(0, 16.4) * mm});
            skPoint(sketch, "E57.0", {"position": v(150, -2.22) * mm});
            skLineSegment(sketch, "E58", {"start": v(150, -2.22) * mm, "end": v(150, -1.22) * mm});
            skLineSegment(sketch, "E59", {"start": v(150, -2.22) * mm, "end": v(0, -2.22) * mm});
            skPoint(sketch, "E60.newPointA", {"position": v(0, 16.4) * mm});
            skPoint(sketch, "E60.newPointB", {"position": v(1, 16.4) * mm});
            skArc(sketch, "E60.filletArc", {"start": v(10, 16.4) * mm, "mid": v(2.93, 13.47) * mm, "end": v(0, 6.4) * mm});
            skPoint(sketch, "E61.newPointA", {"position": v(150, 16.4) * mm});
            skPoint(sketch, "E61.newPointB", {"position": v(149, 16.4) * mm});
            skArc(sketch, "E61.filletArc", {"start": v(150, 6.4) * mm, "mid": v(147.07, 13.47) * mm, "end": v(140, 16.4) * mm});
            skSolve(sketch);
        }
        {
            var Q0;
            {var subQ10=sQuery(id+"F19.wireOp",EDGE,"E53.0");Q0=makeQuery(id+"F19.imprint","IMPRINT",FACE,{"disambiguationData":[TD([[makeQuery(id+"F19.imprint","IMPRINT",EDGE,{"derivedFrom":subQ10}),-1.0]])]});}
            var Q1;
            Q1=makeQuery(id+"F19.imprint","IMPRINT",FACE,{"disambiguationData":[TD([[makeQuery(id+"F19.imprint","IMPRINT",EDGE,{"derivedFrom":makeQuery(id+"F18.boolean.opBoolean","COPY",EDGE,{"derivedFrom":makeQuery(id+"F18.opExtrude","CAP_EDGE",EDGE,{"disambiguationData":[OSD([sQuery(id+"F17.wireOp",EDGE,"E45.MirrorCS")])],"isStart":true})})}),-1.0]])]});
            var Q2;
            {var subQ0=sQuery(id+"F19.wireOp",EDGE,"E53.1");Q2=makeQuery(id+"F19.imprint","IMPRINT",FACE,{"disambiguationData":[TD([[makeQuery(id+"F19.imprint","IMPRINT",EDGE,{"derivedFrom":subQ0}),-1.0]])]});}
            var Q3;
            Q3=makeQuery(id+"F19.imprint","IMPRINT",FACE,{"disambiguationData":[TD([[makeQuery(id+"F19.imprint","IMPRINT",EDGE,{"derivedFrom":makeQuery(id+"F18.boolean.opBoolean","COPY",EDGE,{"derivedFrom":makeQuery(id+"F18.opExtrude","CAP_EDGE",EDGE,{"disambiguationData":[OSD([sQuery(id+"F17.wireOp",EDGE,"E45.MirrorCS")])],"isStart":true})})}),1.0]])]});
            extrude(context, id + "F20", {"entities" : qUnion([Q0, Q1, Q2, Q3]), "operationType" : NewBodyOperationType.INTERSECT, "endBound" : BoundingType.THROUGH_ALL, "oppositeDirection" : true, "depth" : 25 * mm, "offsetDistance" : 25 * mm});
        }
    });
